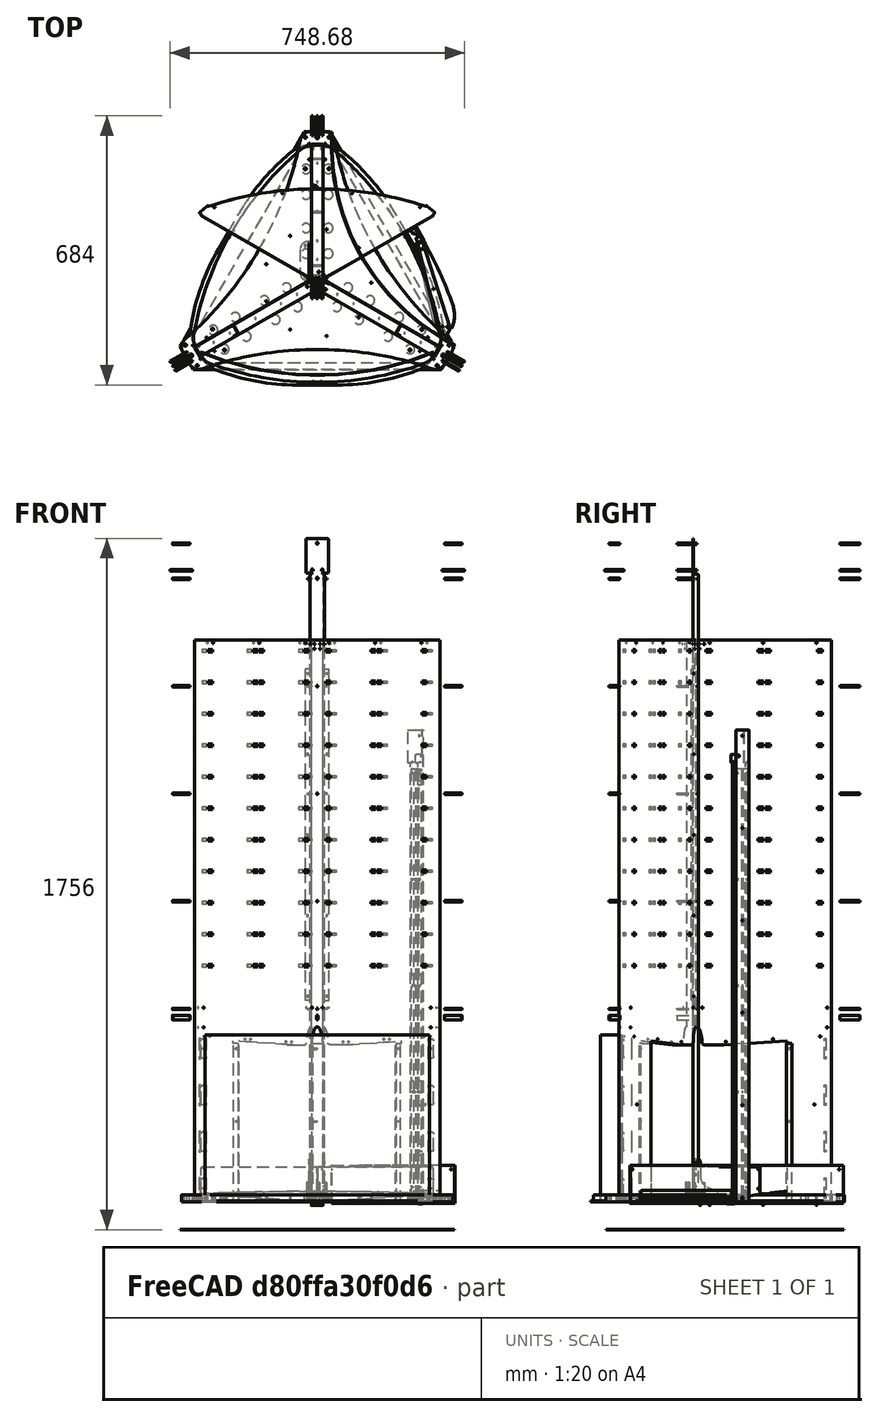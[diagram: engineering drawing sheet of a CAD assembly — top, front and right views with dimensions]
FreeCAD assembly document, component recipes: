
FREECAD ASSEMBLY — COMPONENT RECIPES ("composit_full_size3_door")

This assembly document has 79 components, labeled P0..P78 below (a component is one placed body or linked part). 75 of them carry a construction recipe — the FreeCAD feature program that regenerates the part from scratch, quoted from this document or its linked companion documents; the rest are supplied as boundary geometry only. No exploded tour is included for this assembly.
NOTE — document 2 of 3 of this assembly tour. The two overview renders and the header above are repeated from document 1; the component sections below continue where the previous document stopped.
COMPONENT P41 — recipe-attached ("top_bottom001", modeled in this document).
Construction recipe (the document's own serialized feature program — sketch geometry with constraints, then the solid features built on it; lengths are millimeters unless a unit is written):

FEATURE [PartDesign::SubShapeBinder] Binder007
  BindCopyOnChange = 0
  BindMode = 0
  ClaimChildren = true
  Fuse = false
  MakeFace = true
  OffsetFill = false
  OffsetIntersection = false
  OffsetJoinType = 0
  OffsetOpenResult = false
  PartialLoad = false
  Relative = false
  Support = -> [Compound011]
  _Version = 2
FEATURE [PartDesign::Pad] Pad005
  Direction = (0,0,1)
  Length = 3
  Length2 = 10
  Profile = -> Binder007
  Suppressed = false
  Type = 0
FEATURE [Sketcher::SketchObject] Sketch025
  AttachmentSupport = -> [XY_Plane007]
  FullyConstrained = true
  MapMode = 5
FEATURE [PartDesign::SubShapeBinder] Binder021
  BindCopyOnChange = 0
  BindMode = 0
  ClaimChildren = true
  Fuse = false
  MakeFace = true
  OffsetFill = false
  OffsetIntersection = false
  OffsetJoinType = 0
  OffsetOpenResult = false
  PartialLoad = false
  Relative = false
  Support = -> [Compound014]
  _Version = 2
FEATURE [PartDesign::Pocket] Pocket006
  BaseFeature = -> Pad005
  Direction = (0,0,-1)
  Length = 5
  Length2 = 5
  Midplane = true
  Profile = -> Binder021
  Suppressed = false
  Type = 1
FEATURE [Sketcher::SketchObject] Sketch027
  AttachmentSupport = -> [XY_Plane007]
  FullyConstrained = true
  MapMode = 5
  sketch-geometry (1):
    g0: Circle CenterX=0 CenterY=40 CenterZ=0 NormalX=0 NormalY=0 NormalZ=1 AngleXU=0 Radius=4
  constraints (3):
    c: PointOnObject(g0,g-2)
    c: Diameter(g0) = 8
    c: DistanceY(g0) = 40
FEATURE [PartDesign::SubShapeBinder] Binder023
  BindCopyOnChange = 0
  BindMode = 0
  ClaimChildren = true
  Context = -> Body004 [Binder023.]
  Fuse = false
  MakeFace = true
  OffsetFill = false
  OffsetIntersection = false
  OffsetJoinType = 0
  OffsetOpenResult = false
  PartialLoad = false
  Relative = true
  Support = -> [Clone005]
  _Version = 2
FEATURE [Sketcher::SketchObject] Sketch028
  AttachmentSupport = -> [XY_Plane007]
  ExternalGeometry = -> [Binder023]
  FullyConstrained = true
  MapMode = 5
  expr: Constraints[9] = <<Properties>>.rivet_d
  sketch-geometry (10):
    g0: Circle CenterX=0 CenterY=59 CenterZ=0 NormalX=0 NormalY=0 NormalZ=1 AngleXU=0 Radius=1.7
    g1: Circle CenterX=0 CenterY=106.372 CenterZ=0 NormalX=0 NormalY=0 NormalZ=1 AngleXU=0 Radius=1.7
    g2: Circle CenterX=0 CenterY=181.372 CenterZ=0 NormalX=0 NormalY=0 NormalZ=1 AngleXU=0 Radius=1.7
    g3: Circle CenterX=0 CenterY=256.372 CenterZ=0 NormalX=0 NormalY=0 NormalZ=1 AngleXU=0 Radius=1.7
    g4: Circle CenterX=0 CenterY=303.743 CenterZ=0 NormalX=0 NormalY=0 NormalZ=1 AngleXU=0 Radius=1.7
    g5: LineSegment StartX=28.3 StartY=73.8716 StartZ=0 EndX=28.3 EndY=106.372 EndZ=0
    g6: LineSegment StartX=28.3 StartY=106.372 StartZ=0 EndX=28.3 EndY=138.872 EndZ=0
    g7: LineSegment StartX=28.3 StartY=138.872 StartZ=0 EndX=28.3 EndY=181.372 EndZ=0
    g8: LineSegment StartX=28.3 StartY=181.372 StartZ=0 EndX=28.3 EndY=223.872 EndZ=0
    g9: LineSegment StartX=28.3 StartY=223.872 StartZ=0 EndX=28.3 EndY=256.372 EndZ=0
  constraints (24):
    c: PointOnObject(g0,g-2)
    c: PointOnObject(g1,g-2)
    c: PointOnObject(g2,g-2)
    c: PointOnObject(g3,g-2)
    c: DistanceY(g0) = 59
    c: Equal(g0, g1-g4) x4
    c: Diameter(g0) = 3.4
    c: Coincident(g5,g-3)
    c: Vertical(g5)
    c: Coincident(g5,g6)
    c: Coincident(g6,g-4)
    c: Coincident(g6,g7)
    c: Vertical(g7)
    c: Coincident(g7,g8)
    c: Coincident(g8,g-5)
    c: Coincident(g8,g9)
    c: Vertical(g9)
    c: Equal(g5,g6)
    c: Equal(g6,g9)
    c: Equal(g7,g8)
    c: Horizontal(g2,g7)
    c: Horizontal(g1,g5)
    c: Horizontal(g3,g9)
    c: Symmetric(g0,g4,g2)
FEATURE [PartDesign::Hole] Hole003
  BaseFeature = -> Pocket006
  CustomThreadClearance = 0
  Depth = 25
  DepthType = 0
  Diameter = 3.4
  DrillForDepth = false
  DrillPoint = 1
  DrillPointAngle = 118
  HoleCutCountersinkAngle = 90
  HoleCutCustomValues = false
  HoleCutDepth = 0
  HoleCutDiameter = 6.1
  HoleCutType = 0
  ModelThread = false
  Profile = -> Sketch028
  Reversed = true
  Suppressed = false
  Tapered = false
  TaperedAngle = 90
  ThreadClass = 0
  ThreadDepth = 25
  ThreadDepthType = 0
  ThreadDirection = 0
  ThreadFit = 0
  ThreadSize = 0
  ThreadType = 0
  Threaded = false
  UseCustomThreadClearance = false
  expr: Diameter = <<Properties>>.rivet_d
FEATURE [Part::Compound] Compound048  label="top_bottom_cut1"
  Links = -> [Extrude016,Extrude017]
FEATURE [Part::FeaturePython] Connect  label="top_bottom_cut1_refined"  # WARN: FeaturePython — macro-defined, semantics opaque (R4)
  Objects = -> [Compound048]
  Refine = true
  Tolerance = 0
FEATURE [PartDesign::Boolean] Boolean033
  BaseFeature = -> Hole003
  Group = -> [Compound081]
  Suppressed = false
  Type = 1
  UsePlacement = false
FEATURE [PartDesign::FeatureSubtractivePython] PDW_Common_Sub  # link proxy (typed FeaturePython)
  BaseFeature = -> Boolean033
  Body = Body004
  ClaimChildren = true
  EditPlacementAdjustments = false
  Enabled = 1
  LinkedObject = -> Connect
  MeshTolerance = 0.1
  PatternBaseOffset = 0
  PatternBaseScale = 1
  PatternBaseScaleXYZ = (1,1,1)
  PatternOffsetCut = false
  PatternOffsetIntersection = false
  PatternOffsetJoin = 0
  PatternOffsetMode = 0
  PatternOffsetSelfIntersection = false
  PatternOperation = 3
  PatternOperationDefault = Common
  PatternScaleCut = false
  PatternShapeOffset = 0
  PatternShapeScale = 1
  PatternShapeScaleXYZ = (1,1,1)
  PatternTool = -> Compound048
  PatternToolOffset = 0
  PatternToolScale = 1
  PatternToolScaleXYZ = (1,1,1)
  Refine = true
  RefineMesh = true
  ShapeManagement = 1
  ShowMeshProps = false
  ShowOffsetProps = false
  ShowScaleProps = false
  ShowWarnings = true
  Suppressed = false
  TipBase = -> Boolean033
  TipBaseOffset = 0
  TipBaseScale = 1
  TipBaseScaleXYZ = (1,1,1)
  TipOffsetCut = false
  TipOffsetIntersection = false
  TipOffsetJoin = 0
  TipOffsetMode = 0
  TipOffsetSelfIntersection = false
  TipOperation = 1
  TipOperationDefault = Common
  TipScaleCut = false
  TipShapeOffset = 0
  TipShapeScale = 1
  TipShapeScaleXYZ = (1,1,1)
  TipTool = -> Connect
  TipToolOffset = 0
  TipToolScale = 1
  TipToolScaleXYZ = (1,1,1)
  Type = Subtractive
  UsePatternBaseAddSubShape = false
  UsePatternToolAddSubShape = false
  UseTipBaseAddSubShape = true
  UseTipToolAddSubShape = true
  Version = 0.2023.08.13
FEATURE [PartDesign::CoordinateSystem] Local_CS029  label="dropper_fix_bottom_outer_LCS"
  AttacherType = Attacher::AttachEngine3D
  AttachmentSupport = -> [XY_Plane007]
  MapMode = 5
FEATURE [PartDesign::CoordinateSystem] Local_CS030  label="dropper_fix_bottom_inner_LCS"
  AttacherType = Attacher::AttachEngine3D
  AttachmentOffset = pos=(0,0,3) rot=(0,0,1;0rad)
  AttachmentSupport = -> [XY_Plane007]
  MapMode = 5
  Placement = pos=(0,0,3) rot=(0,0,1;0rad)
FEATURE [PartDesign::Body] Body004  label="dropper_fix_bottom"
  Group = -> [Binder007,Pad005,Sketch025,Binder021,Pocket006,Sketch027,Sketch028,Binder023,Hole003,Boolean033,PDW_Common_Sub,Compound048,Connect,Local_CS029,Local_CS030]
  Origin = -> Origin007
  Tip = -> PDW_Common_Sub
COMPONENT P42 — recipe-attached ("cap_outer_material_0.30ansi001", modeled in this document).
Construction recipe (the document's own serialized feature program — sketch geometry with constraints, then the solid features built on it; lengths are millimeters unless a unit is written):

FEATURE [PartDesign::SubShapeBinder] Binder012
  BindCopyOnChange = 0
  BindMode = 0
  ClaimChildren = true
  Fuse = false
  MakeFace = true
  OffsetFill = false
  OffsetIntersection = false
  OffsetJoinType = 0
  OffsetOpenResult = false
  PartialLoad = false
  Placement = pos=(0,0,40) rot=(0,0,1;0rad)
  Relative = false
  Support = -> [Compound012]
  _Version = 2
FEATURE [PartDesign::SubShapeBinder] Binder013
  BindCopyOnChange = 0
  BindMode = 0
  ClaimChildren = true
  Fuse = false
  MakeFace = true
  OffsetFill = false
  OffsetIntersection = false
  OffsetJoinType = 0
  OffsetOpenResult = false
  PartialLoad = false
  Placement = pos=(0,0,40) rot=(0,0,1;0rad)
  Relative = false
  Support = -> [Compound013]
  _Version = 2
FEATURE [PartDesign::FeaturePython] BaseBend007  # WARN: FeaturePython — macro-defined, semantics opaque (R4)
  BendSide = 1
  BendSketch = -> Binder012
  MidPlane = false
  Reverse = true
  Suppressed = false
  length = 100
  radius = 0.1
  thickness = 0.3
  expr: radius = composit_properties#<<Properties>>.bend_r
  expr: thickness = composit_properties#<<Properties>>.al_thickness
FEATURE [PartDesign::FeaturePython] Bend001  # WARN: FeaturePython — macro-defined, semantics opaque (R4)
  AutoMiter = false
  BaseFeature = -> BaseBend007
  BendType = 0
  LengthList = [47]
  LengthSpec = 1
  ReliefFactor = 0.7
  Suppressed = false
  UseReliefFactor = false
  angle = 90
  baseObject = -> BaseBend007 [Edge14,Edge30,Edge46,Edge62,Edge70,Edge86,Edge102,Edge116]
  bendAList = [90]
  extend1 = 0
  extend2 = 0
  gap1 = 0
  gap2 = 0
  invert = false
  kfactor = 0.5
  length = 47
  maxExtendDist = 5
  minGap = 0.1
  minReliefGap = 1
  miterangle1 = 0
  miterangle2 = 0
  offset = 0
  radius = 0.1
  reliefType = 0
  reliefd = 1
  reliefw = 0.8
  sketchflip = false
  sketchinvert = false
  unfold = false
  expr: radius = BaseBend007.radius
FEATURE [PartDesign::Pocket] Pocket002
  BaseFeature = -> Bend001
  Direction = (0,0,-1)
  Length = 5
  Length2 = 5
  Profile = -> Binder013 [Face1]
  Refine = true
  Reversed = true
  Suppressed = false
  Type = 1
FEATURE [PartDesign::SubShapeBinder] Binder014
  BindCopyOnChange = 0
  BindMode = 0
  ClaimChildren = true
  Context = -> Link012 [Binder014.]
  Fuse = false
  MakeFace = true
  OffsetFill = false
  OffsetIntersection = false
  OffsetJoinType = 0
  OffsetOpenResult = false
  PartialLoad = false
  Relative = true
  Support = -> [Sketch019]
  _Version = 2
FEATURE [Sketcher::SketchObject] Sketch020
  AttachmentSupport = -> [XY_Plane005]
  FullyConstrained = true
  MapMode = 5
  expr: Constraints[10] = composit_properties#<<Properties>>.bend_r + composit_properties#<<Properties>>.al_thickness
  sketch-geometry (5):
    g0: ArcOfCircle CenterX=0 CenterY=0.46188 CenterZ=0 NormalX=0 NormalY=0 NormalZ=1 AngleXU=0 Radius=5 StartAngle=0.523599 EndAngle=2.61799
    g1: LineSegment StartX=0 StartY=0 StartZ=0 EndX=4.53013 EndY=2.61547 EndZ=0
    g2: LineSegment StartX=4.53013 StartY=2.61547 StartZ=0 EndX=4.33013 EndY=2.96188 EndZ=0
    g3: LineSegment StartX=0 StartY=0 StartZ=0 EndX=-4.53013 EndY=2.61547 EndZ=0
    g4: LineSegment StartX=-4.53013 StartY=2.61547 StartZ=0 EndX=-4.33013 EndY=2.96188 EndZ=0
  constraints (13):
    c: PointOnObject(g0,g-2)
    c: Coincident(g1,g-1)
    c: Coincident(g2,g1)
    c: Coincident(g3,g1)
    c: Coincident(g4,g3)
    c: Perpendicular(g3,g4)
    c: Perpendicular(g1,g2)
    c: Tangent(g2,g0) = -1.5708
    c: Tangent(g4,g0) = 1.5708
    c: Equal(g4,g2)
    c: Distance(g2) = 0.4
    c: Diameter(g0) = 10
    c: Angle(g1,g3) = 2.0944
FEATURE [PartDesign::SubShapeBinder] Binder015
  BindCopyOnChange = 0
  BindMode = 0
  ClaimChildren = false
  Context = -> Link012 [Binder015.]
  Fuse = false
  MakeFace = true
  OffsetFill = false
  OffsetIntersection = false
  OffsetJoinType = 0
  OffsetOpenResult = false
  PartialLoad = false
  Relative = true
  Support = -> [Sketch002]
  _Version = 2
  expr: Support = <<dropper_fix_sketch>>._self
FEATURE [Sketcher::SketchObject] Sketch022  label="cap_outer_shape"
  AttachmentSupport = -> [YZ_Plane005]
  ExternalGeometry = -> [Binder012]
  FullyConstrained = true
  MapMode = 5
  Placement = pos=(0,0,0) rot=(0.57735,0.57735,0.57735;2.0944rad)
  expr: Constraints[11] = composit_properties#<<Properties>>.bend_r + composit_properties#<<Properties>>.al_thickness
  expr: Constraints[9] = composit_properties#<<Properties>>.bend_r + composit_properties#<<Properties>>.al_thickness + 0.01 mm
  sketch-geometry (5):
    g0: LineSegment StartX=351.882 StartY=40.41 StartZ=0 EndX=0 EndY=40.41 EndZ=0
    g1: LineSegment StartX=0 StartY=40.41 StartZ=0 EndX=0 EndY=0 EndZ=0
    g2: LineSegment StartX=0 StartY=0 StartZ=0 EndX=351.882 EndY=0 EndZ=0
    g3: LineSegment StartX=351.882 StartY=0 StartZ=0 EndX=351.882 EndY=40.41 EndZ=0
    g4: GeomPoint X=351.872 Y=40.4 Z=0
  constraints (14):
    c: Coincident(g0,g1)
    c: Coincident(g1,g2)
    c: Coincident(g2,g3)
    c: Coincident(g3,g0)
    c: Horizontal(g0)
    c: Horizontal(g2)
    c: Vertical(g1)
    c: Vertical(g3)
    c: Coincident(g1,g-1)
    c: DistanceY(g-3,g0) = 0.41
    c: DistanceX(g-3,g0) = 0.01
    c: DistanceY(g-3,g4) = 0.4
    c: Vertical(g-3,g4)
    c: DistanceY(g4) = 40.4  'height'
FEATURE [Part::FeaturePython] WireFilter002  # WARN: FeaturePython — macro-defined, semantics opaque (R4)
  AttacherType = Attacher::AttachEngine3D
  ClaimChildren = true
  ColorKeyCount = 8
  Colorize = true
  FaceMaker = 5
  FixNormal = false
  FollowSource = true
  InvertedFaceScale = 5
  MaxWires = 25
  Normal = (1,0,0)
  OffsetFill = false
  OffsetIntersection = false
  OffsetJoin = 0
  OffsetOpenResult = false
  Scale = (1,1,1)
  SelectEdges = false
  Source = -> Sketch022
  UniformScale = 1
  UseDefault = false
  UseSelected = true
  UseSelectedEdges = false
  Version = 0.2022.02.09
  WireOrder = [1]
FEATURE [PartDesign::SubShapeBinder] Binder132
  BindCopyOnChange = 0
  BindMode = 0
  ClaimChildren = true
  Fuse = false
  MakeFace = true
  OffsetFill = false
  OffsetIntersection = false
  OffsetJoinType = 0
  OffsetOpenResult = false
  PartialLoad = false
  Relative = false
  Support = -> [Sketch017]
  _Version = 2
FEATURE [PartDesign::Pocket] Pocket125
  BaseFeature = -> Pocket002
  Direction = (0,0,-1)
  Length = 5
  Length2 = 5
  Midplane = true
  Profile = -> Binder014
  Suppressed = false
  Type = 1
FEATURE [PartDesign::Pocket] Pocket003
  BaseFeature = -> Pocket125
  Direction = (0,0,-1)
  Length = 5
  Length2 = 5
  Midplane = true
  Profile = -> Sketch020
  ReferenceAxis = -> Sketch020 [N_Axis]
  Suppressed = false
  Type = 1
FEATURE [PartDesign::Mirrored] Mirrored
  BaseFeature = -> Pocket003
  MirrorPlane = -> YZ_Plane005
  Suppressed = false
FEATURE [PartDesign::Pocket] Pocket005
  BaseFeature = -> Mirrored
  Direction = (-1,0,0)
  Length = 5
  Length2 = 5
  Midplane = true
  Profile = -> WireFilter002
  Suppressed = false
  Type = 1
FEATURE [PartDesign::Boolean] Boolean032
  BaseFeature = -> Pocket005
  Group = -> [Compound080]
  Suppressed = false
  Type = 1
  UsePlacement = false
FEATURE [PartDesign::Body] Body002  label="cap_outer_material_0.30ansi"
  Group = -> [Binder012,Binder013,BaseBend007,Bend001,Pocket002,Binder014,Sketch020,Pocket125,Pocket003,Binder015,Mirrored,Sketch022,WireFilter002,Pocket005,Binder132,Boolean032]
  Origin = -> Origin005
  Tip = -> Boolean032
COMPONENT P43 — recipe-attached ("cap_inner2_material_0.30ansi001", modeled in this document).
Construction recipe (the document's own serialized feature program — sketch geometry with constraints, then the solid features built on it; lengths are millimeters unless a unit is written):

FEATURE [PartDesign::SubShapeBinder] Binder018
  BindCopyOnChange = 0
  BindMode = 0
  ClaimChildren = false
  Fuse = false
  MakeFace = true
  OffsetFill = false
  OffsetIntersection = false
  OffsetJoinType = 0
  OffsetOpenResult = false
  PartialLoad = false
  Relative = false
  Support = -> [Body002[BaseBend007.Binder012.Compound012.Part__Mirroring006.Sketch016.]]
  _Version = 2
FEATURE [PartDesign::SubShapeBinder] Binder019
  BindCopyOnChange = 0
  BindMode = 0
  ClaimChildren = false
  Fuse = false
  MakeFace = false
  OffsetFill = false
  OffsetIntersection = false
  OffsetJoinType = 0
  OffsetOpenResult = false
  PartialLoad = false
  Relative = false
  Support = -> [Sketch019]
  _Version = 2
FEATURE [Sketcher::SketchObject] Sketch024
  AttachmentSupport = -> [XY_Plane023]
  ExternalGeometry = -> [Binder019,Binder018]
  FullyConstrained = true
  MapMode = 5
  expr: Constraints[10] = composit_properties#<<Properties>>.thickness + composit_properties#<<Properties>>.al_thickness + composit_properties#<<Properties>>.bend_r
  sketch-geometry (5):
    g0: LineSegment StartX=-41.7 StartY=272.288 StartZ=0 EndX=-41.7 EndY=289.736 EndZ=0
    g1: LineSegment StartX=-41.7 StartY=289.736 StartZ=0 EndX=41.7 EndY=289.736 EndZ=0
    g2: LineSegment StartX=41.7 StartY=289.736 StartZ=0 EndX=41.7 EndY=272.288 EndZ=0
    g3: LineSegment StartX=41.7 StartY=272.288 StartZ=0 EndX=-41.7 EndY=272.288 EndZ=0
    g4: GeomPoint X=0 Y=281.012 Z=0
  constraints (13):
    c: Coincident(g0,g1)
    c: Coincident(g1,g2)
    c: Coincident(g2,g3)
    c: Coincident(g3,g0)
    c: Horizontal(g1)
    c: Horizontal(g3)
    c: Vertical(g0)
    c: Vertical(g2)
    c: Symmetric(g1,g0,g4)
    c: PointOnObject(g4,g-2)
    c: DistanceX(g1,g-4) = 3.4
    c: DistanceY(g2,g-3) = 5
    c: DistanceY(g1,g-4) = 3
FEATURE [PartDesign::FeaturePython] BaseBend008  # WARN: FeaturePython — macro-defined, semantics opaque (R4)
  BendSide = 0
  BendSketch = -> Sketch024
  MidPlane = false
  Reverse = false
  Suppressed = false
  length = 100
  radius = 0.1
  thickness = 0.3
  expr: radius = composit_properties#<<Properties>>.bend_r
  expr: thickness = composit_properties#<<Properties>>.al_thickness
FEATURE [Sketcher::SketchObject] Sketch217
  AttachmentSupport = -> [XY_Plane023]
  ExternalGeometry = -> [Sketch024,Binder018]
  FullyConstrained = true
  MapMode = 5
  sketch-geometry (6):
    g0: LineSegment StartX=41.7 StartY=289.736 StartZ=0 EndX=14.25 EndY=348.472 EndZ=0
    g1: LineSegment StartX=0 StartY=348.472 StartZ=0 EndX=14.25 EndY=348.472 EndZ=0
    g2: LineSegment StartX=14.25 StartY=351.872 StartZ=0 EndX=14.25 EndY=348.472 EndZ=0
    g3: LineSegment StartX=14.25 StartY=348.472 StartZ=0 EndX=17.3302 EndY=349.911 EndZ=0
    g4: LineSegment StartX=0 StartY=348.472 StartZ=0 EndX=0 EndY=289.736 EndZ=0
    g5: LineSegment StartX=0 StartY=289.736 StartZ=0 EndX=41.7 EndY=289.736 EndZ=0
  constraints (17):
    c: Coincident(g0,g-3)
    c: PointOnObject(g1,g-2)
    c: Coincident(g1,g0)
    c: Horizontal(g1)
    c: Coincident(g2,g0)
    c: Coincident(g2,g3)
    c: PointOnObject(g3,g-4)
    c: Perpendicular(g0,g3)
    c: Perpendicular(g1,g2)
    c: Equal(g3,g2)
    c: DistanceY(g2,g2) = 3.4
    c: Horizontal(g2,g-4)
    c: Coincident(g4,g1)
    c: PointOnObject(g4,g-3)
    c: Vertical(g4)
    c: Coincident(g5,g4)
    c: Coincident(g5,g0)
FEATURE [PartDesign::Pad] Pad033
  BaseFeature = -> BaseBend008
  Direction = (0,0,1)
  Length = 0.3
  Length2 = 10
  Profile = -> Sketch217
  ReferenceAxis = -> Sketch217 [N_Axis]
  Suppressed = false
  Type = 0
FEATURE [PartDesign::Mirrored] Mirrored016
  BaseFeature = -> Pad033
  MirrorPlane = -> Sketch217 [V_Axis]
  Originals = -> [Pad033]
  Suppressed = false
FEATURE [PartDesign::Hole] Hole002
  BaseFeature = -> Mirrored016
  CustomThreadClearance = 0
  Depth = 25
  DepthType = 0
  Diameter = 3.4
  DrillForDepth = false
  DrillPoint = 1
  DrillPointAngle = 118
  HoleCutCountersinkAngle = 90
  HoleCutCustomValues = false
  HoleCutDepth = 0
  HoleCutDiameter = 6.1
  HoleCutType = 0
  ModelThread = false
  Profile = -> Binder019
  Refine = true
  Reversed = true
  Suppressed = false
  Tapered = false
  TaperedAngle = 90
  ThreadClass = 0
  ThreadDepth = 25
  ThreadDepthType = 0
  ThreadDirection = 0
  ThreadFit = 0
  ThreadSize = 0
  ThreadType = 0
  Threaded = false
  UseCustomThreadClearance = false
  expr: Diameter = <<Properties>>.rivet_d
FEATURE [PartDesign::Body] Body016  label="cap_inner2_material_0.30ansi"
  Group = -> [Binder018,Binder019,Sketch024,BaseBend008,Sketch217,Pad033,Mirrored016,Hole002]
  Origin = -> Origin023
  Tip = -> Hole002
COMPONENT P44 — recipe-attached ("top_connector_material_0.30ansi001", modeled in this document).
Construction recipe (the document's own serialized feature program — sketch geometry with constraints, then the solid features built on it; lengths are millimeters unless a unit is written):

FEATURE [Sketcher::SketchObject] Sketch029  label="top_connector_base_sketch"
  AttachmentOffset = pos=(0,0,-35) rot=(0,0,1;0rad)
  AttachmentSupport = -> [XZ_Plane024]
  FullyConstrained = true
  MapMode = 5
  Placement = pos=(0,35,-7.8e-15) rot=(1,0,0;1.5708rad)
  expr: .Constraints.width = <<Properties>>.inner_width
  sketch-geometry (5):
    g0: LineSegment StartX=-11.5 StartY=-13 StartZ=0 EndX=-11.5 EndY=-1.95e-14 EndZ=0
    g1: LineSegment StartX=-11.5 StartY=-1.95e-14 StartZ=0 EndX=11.5 EndY=-1.95e-14 EndZ=0
    g2: LineSegment StartX=11.5 StartY=-1.95e-14 StartZ=0 EndX=11.5 EndY=-13 EndZ=0
    g3: LineSegment StartX=11.5 StartY=-13 StartZ=0 EndX=-11.5 EndY=-13 EndZ=0
    g4: GeomPoint X=-3.6e-15 Y=-6.5 Z=0
  constraints (13):
    c: Coincident(g0,g1)
    c: Coincident(g1,g2)
    c: Coincident(g2,g3)
    c: Coincident(g3,g0)
    c: Horizontal(g1)
    c: Horizontal(g3)
    c: Vertical(g0)
    c: Vertical(g2)
    c: Symmetric(g1,g0,g4)
    c: PointOnObject(g4,g-2)
    c: PointOnObject(g1,g-1)
    c: DistanceX(g1,g1) = 23  'width'
    c: DistanceY(g2,g2) = 13  'height'
FEATURE [PartDesign::FeaturePython] BaseBend009  # WARN: FeaturePython — macro-defined, semantics opaque (R4)
  BendSide = 0
  BendSketch = -> Sketch029
  MidPlane = false
  Reverse = true
  Suppressed = false
  length = 283.743
  radius = 0.1
  thickness = 0.3
  expr: radius = composit_properties#<<Properties>>.bend_r
  expr: thickness = composit_properties#<<Properties>>.al_thickness
FEATURE [PartDesign::SubShapeBinder] Binder029
  BindCopyOnChange = 0
  BindMode = 0
  ClaimChildren = false
  Context = -> Body017 [Binder029.]
  Fuse = false
  MakeFace = true
  OffsetFill = false
  OffsetIntersection = false
  OffsetJoinType = 0
  OffsetOpenResult = false
  PartialLoad = false
  Relative = true
  Support = -> [Sketch027]
  _Version = 2
  expr: Support = Sketch027._self
FEATURE [PartDesign::SubShapeBinder] Binder030
  BindCopyOnChange = 0
  BindMode = 0
  ClaimChildren = false
  Context = -> Body017 [Binder030.]
  Fuse = false
  MakeFace = true
  OffsetFill = false
  OffsetIntersection = false
  OffsetJoinType = 0
  OffsetOpenResult = false
  PartialLoad = false
  Relative = true
  Support = -> [Sketch028]
  _Version = 2
  expr: Support = Sketch028._self
FEATURE [PartDesign::Hole] Hole004
  BaseFeature = -> BaseBend009
  CustomThreadClearance = 0
  Depth = 25
  DepthType = 0
  Diameter = 3.4
  DrillForDepth = false
  DrillPoint = 1
  DrillPointAngle = 118
  HoleCutCountersinkAngle = 90
  HoleCutCustomValues = false
  HoleCutDepth = 0
  HoleCutDiameter = 6.1
  HoleCutType = 0
  ModelThread = false
  Profile = -> Binder030
  Suppressed = false
  Tapered = false
  TaperedAngle = 90
  ThreadClass = 0
  ThreadDepth = 25
  ThreadDepthType = 0
  ThreadDirection = 0
  ThreadFit = 0
  ThreadSize = 0
  ThreadType = 0
  Threaded = false
  UseCustomThreadClearance = false
  expr: Diameter = <<Properties>>.rivet_d
FEATURE [Sketcher::SketchObject] Sketch048
  AttachmentSupport = -> [YZ_Plane024]
  FullyConstrained = true
  MapMode = 5
  Placement = pos=(0,0,0) rot=(0.57735,0.57735,0.57735;2.0944rad)
  expr: Constraints[5] = -<<top_connector_base_sketch>>.Constraints.height
  expr: Constraints[7] = -<<top_connector_base_sketch>>.AttachmentOffset.Base.z
  sketch-geometry (3):
    g0: ArcOfCircle CenterX=42 CenterY=-6 CenterZ=0 NormalX=0 NormalY=0 NormalZ=1 AngleXU=0 Radius=7 StartAngle=3.14159 EndAngle=4.71239
    g1: LineSegment StartX=42 StartY=-13 StartZ=0 EndX=35 EndY=-13 EndZ=0
    g2: LineSegment StartX=35 StartY=-6 StartZ=0 EndX=35 EndY=-13 EndZ=0
  constraints (8):
    c: Horizontal(g1)
    c: Coincident(g2,g1)
    c: Vertical(g2)
    c: Tangent(g1,g0) = 1.5708
    c: Tangent(g2,g0) = -1.5708
    c: DistanceY(g1) = -13
    c: DistanceY(g0) = -6
    c: DistanceX(g1) = 35
FEATURE [PartDesign::Boolean] Boolean007
  BaseFeature = -> Hole004
  Group = -> [Compound078]
  Suppressed = false
  Type = 1
  UsePlacement = false
  expr: Group = <<top_connector_cut1>>._self
FEATURE [PartDesign::Pocket] Pocket027
  BaseFeature = -> Boolean007
  Direction = (-1,0,0)
  Length = 5
  Length2 = 5
  Midplane = true
  Profile = -> Sketch048
  ReferenceAxis = -> Sketch048 [N_Axis]
  Suppressed = false
  Type = 1
FEATURE [PartDesign::Body] Body017  label="top_connector_material_0.30ansi"
  Group = -> [Sketch029,BaseBend009,Binder029,Binder030,Hole004,Boolean007,Sketch048,Pocket027]
  Origin = -> Origin024
  Tip = -> Pocket027
COMPONENT P45 — recipe-attached ("cap_inner1_material_0.30ansi001", modeled in this document).
Construction recipe (the document's own serialized feature program — sketch geometry with constraints, then the solid features built on it; lengths are millimeters unless a unit is written):

FEATURE [PartDesign::SubShapeBinder] Binder016
  BindCopyOnChange = 0
  BindMode = 0
  ClaimChildren = true
  Fuse = false
  MakeFace = false
  OffsetFill = false
  OffsetIntersection = false
  OffsetJoinType = 0
  OffsetOpenResult = false
  PartialLoad = false
  Relative = false
  Support = -> [Sketch019]
  _Version = 2
FEATURE [PartDesign::SubShapeBinder] Binder020
  BindCopyOnChange = 0
  BindMode = 0
  ClaimChildren = false
  Context = -> Link015 [Binder020.]
  Fuse = false
  MakeFace = true
  OffsetFill = false
  OffsetIntersection = false
  OffsetJoinType = 0
  OffsetOpenResult = false
  PartialLoad = false
  Relative = true
  Support = -> [Body002[BaseBend007.Binder012.Compound012.Part__Mirroring006.Sketch016.]]
  _Version = 2
FEATURE [Sketcher::SketchObject] Sketch023
  AttachmentSupport = -> [XY_Plane006]
  ExternalGeometry = -> [Binder020]
  FullyConstrained = true
  MapMode = 5
  expr: Constraints[9] = composit_properties#<<Properties>>.thickness + composit_properties#<<Properties>>.bend_r + composit_properties#<<Properties>>.al_thickness
  sketch-geometry (5):
    g0: LineSegment StartX=41.7 StartY=29.0385 StartZ=0 EndX=-41.7 EndY=29.0385 EndZ=0
    g1: LineSegment StartX=-41.7 StartY=29.0385 StartZ=0 EndX=-41.7 EndY=58.0385 EndZ=0
    g2: LineSegment StartX=-41.7 StartY=58.0385 StartZ=0 EndX=41.7 EndY=58.0385 EndZ=0
    g3: LineSegment StartX=41.7 StartY=58.0385 StartZ=0 EndX=41.7 EndY=29.0385 EndZ=0
    g4: GeomPoint X=0 Y=43.5385 Z=0
  constraints (13):
    c: Coincident(g0,g1)
    c: Coincident(g1,g2)
    c: Coincident(g2,g3)
    c: Coincident(g3,g0)
    c: Horizontal(g0)
    c: Horizontal(g2)
    c: Vertical(g1)
    c: Vertical(g3)
    c: DistanceY(g-3,g0) = 3
    c: DistanceX(g0,g-3) = 3.4
    c: PointOnObject(g4,g-2)
    c: Symmetric(g2,g0,g4)
    c: DistanceY(g3,g3) = 29
FEATURE [PartDesign::Pad] Pad007
  Direction = (0,0,1)
  Length = 0.3
  Length2 = 10
  Profile = -> Sketch023
  ReferenceAxis = -> Sketch023 [N_Axis]
  Suppressed = false
  Type = 0
  expr: Length = composit_properties#<<Properties>>.al_thickness
FEATURE [PartDesign::FeaturePython] Bend002  label="cap_inner1_bend"  # WARN: FeaturePython — macro-defined, semantics opaque (R4)
  AutoMiter = true
  BaseFeature = -> Pad007
  BendType = 0
  LengthList = [31]
  LengthSpec = 0
  ReliefFactor = 0.7
  Suppressed = false
  UseReliefFactor = false
  angle = 90
  baseObject = -> Pad007 [Edge12,Edge7]
  bendAList = [90]
  extend1 = 0
  extend2 = 0
  gap1 = 0
  gap2 = 0
  invert = false
  kfactor = 0.5
  length = 31
  maxExtendDist = 5
  minGap = 0.1
  minReliefGap = 1
  miterangle1 = 0
  miterangle2 = 0
  offset = 0
  radius = 0.1
  reliefType = 0
  reliefd = 1
  reliefw = 0.8
  sketchflip = false
  sketchinvert = false
  unfold = false
  expr: length = <<cap_outer_shape>>.Constraints.height - composit_properties#<<Properties>>.thickness - composit_properties#<<Properties>>.al_thickness - composit_properties#<<Properties>>.bend_r - 6 mm
  expr: radius = BaseBend007.radius
FEATURE [PartDesign::Hole] Hole001
  BaseFeature = -> Bend002
  CustomThreadClearance = 0
  Depth = 25
  DepthType = 0
  Diameter = 3.4
  DrillForDepth = false
  DrillPoint = 1
  DrillPointAngle = 118
  HoleCutCountersinkAngle = 90
  HoleCutCustomValues = false
  HoleCutDepth = 0
  HoleCutDiameter = 6.1
  HoleCutType = 0
  ModelThread = false
  Profile = -> Binder016
  Reversed = true
  Suppressed = false
  Tapered = false
  TaperedAngle = 90
  ThreadClass = 0
  ThreadDepth = 25
  ThreadDepthType = 0
  ThreadDirection = 0
  ThreadFit = 0
  ThreadSize = 0
  ThreadType = 0
  Threaded = false
  UseCustomThreadClearance = false
  expr: Diameter = <<Properties>>.rivet_d
FEATURE [PartDesign::Body] Body003  label="cap_inner1_material_0.30ansi"
  Group = -> [Sketch023,Binder016,Binder020,Pad007,Bend002,Hole001]
  Origin = -> Origin006
  Tip = -> Hole001
COMPONENT P46 — same part as P37; its construction recipe is shown at P37.
COMPONENT P47 — recipe-attached ("part2_material_0.30ansi001", modeled in this document).
Construction recipe (the document's own serialized feature program — sketch geometry with constraints, then the solid features built on it; lengths are millimeters unless a unit is written):

FEATURE [PartDesign::SubShapeBinder] Binder001
  BindCopyOnChange = 0
  BindMode = 0
  ClaimChildren = true
  Context = -> Body001 [Binder001.]
  Fuse = false
  MakeFace = true
  OffsetFill = false
  OffsetIntersection = false
  OffsetJoinType = 0
  OffsetOpenResult = false
  PartialLoad = false
  Placement = pos=(0,0,0) rot=(0,0,1;4.18879rad)
  Relative = false
  Support = -> [Array001]
  _Version = 2
  expr: Support = <<2part_base>>._self
FEATURE [PartDesign::FeaturePython] BaseBend001  # WARN: FeaturePython — macro-defined, semantics opaque (R4)
  BendSide = 0
  BendSketch = -> Binder001
  MidPlane = false
  Reverse = false
  Suppressed = false
  length = 1428
  radius = 0.1
  thickness = 0.3
  expr: length = <<Properties>>.total_height
  expr: radius = composit_properties#<<Properties>>.bend_r
  expr: thickness = composit_properties#<<Properties>>.al_thickness
FEATURE [PartDesign::CoordinateSystem] Local_CS027  label="part2_bottom"
  AttacherType = Attacher::AttachEngine3D
  AttachmentOffset = pos=(0,0,0) rot=(0,0,1;2.0944rad)
  AttachmentSupport = -> [XY_Plane001]
  MapMode = 5
  Placement = pos=(0,0,0) rot=(0,0,1;2.0944rad)
FEATURE [PartDesign::CoordinateSystem] Local_CS028
  AttacherType = Attacher::AttachEngine3D
  AttachmentOffset = pos=(0,0,1428) rot=(0,0,1;0rad)
  AttachmentSupport = -> [Local_CS027]
  MapMode = 5
  Placement = pos=(0,0,1428) rot=(0,0,1;2.0944rad)
  expr: .AttachmentOffset.Base.z = <<Properties>>.total_height
FEATURE [PartDesign::Boolean] Boolean
  BaseFeature = -> BaseBend001
  Group = -> [Compound021]
  Refine = true
  Suppressed = false
  Type = 1
  UsePlacement = false
  expr: Group = <<part2_cut1>>._self
FEATURE [PartDesign::Boolean] Boolean003
  BaseFeature = -> Boolean
  Group = -> [Compound007]
  Refine = true
  Suppressed = false
  Type = 0
  UsePlacement = false
  expr: Group = <<part2_fuse1>>._self
FEATURE [PartDesign::Boolean] Boolean006
  BaseFeature = -> Boolean003
  Group = -> [Compound025]
  Suppressed = false
  Type = 1
  UsePlacement = false
  expr: Group = <<part2_cut2>>._self
FEATURE [PartDesign::Body] Body001  label="part2_material_0.30ansi"
  Group = -> [Binder001,BaseBend001,Boolean,Boolean003,Boolean006,Local_CS027,Local_CS028]
  Origin = -> Origin001
  Tip = -> Boolean006
COMPONENT P48 — recipe-attached ("bot_hor_amplifier_material_0.30ansi001", modeled in this document).
Construction recipe (the document's own serialized feature program — sketch geometry with constraints, then the solid features built on it; lengths are millimeters unless a unit is written):

FEATURE [Sketcher::SketchObject] Sketch049
  AttachmentSupport = -> [YZ_Plane030]
  FullyConstrained = true
  MapMode = 5
  Placement = pos=(0,0,0) rot=(0.57735,0.57735,0.57735;2.0944rad)
  expr: Constraints[11] = <<Properties>>.inner_width
  sketch-geometry (5):
    g0: LineSegment StartX=-11.5 StartY=-14 StartZ=0 EndX=-11.5 EndY=0 EndZ=0
    g1: LineSegment StartX=-11.5 StartY=0 StartZ=0 EndX=11.5 EndY=0 EndZ=0
    g2: LineSegment StartX=11.5 StartY=0 StartZ=0 EndX=11.5 EndY=-14 EndZ=0
    g3: LineSegment StartX=11.5 StartY=-14 StartZ=0 EndX=-11.5 EndY=-14 EndZ=0
    g4: GeomPoint X=0 Y=-7 Z=0
  constraints (13):
    c: Coincident(g0,g1)
    c: Coincident(g1,g2)
    c: Coincident(g2,g3)
    c: Coincident(g3,g0)
    c: Horizontal(g1)
    c: Horizontal(g3)
    c: Vertical(g0)
    c: Vertical(g2)
    c: Symmetric(g1,g0,g4)
    c: PointOnObject(g4,g-2)
    c: PointOnObject(g1,g-1)
    c: DistanceX(g1,g1) = 23
    c: DistanceY(g2) = -14
FEATURE [PartDesign::FeaturePython] BaseBend019  # WARN: FeaturePython — macro-defined, semantics opaque (R4)
  BendSide = 0
  BendSketch = -> Sketch049
  MidPlane = true
  Reverse = false
  Suppressed = false
  length = 250
  radius = 0.1
  thickness = 0.3
FEATURE [PartDesign::Boolean] Boolean009
  BaseFeature = -> BaseBend019
  Group = -> [Extrude008]
  Suppressed = false
  Type = 1
  UsePlacement = false
  expr: Group = <<bot_hor_amplifier_extrude>>._self
FEATURE [PartDesign::Body] Body068  label="bot_hor_amplifier_material_0.30ansi"
  Group = -> [BaseBend019,Sketch049,Boolean009]
  Origin = -> Origin030
  Tip = -> Boolean009
COMPONENT P49 — recipe-attached ("star_material_0.30ansi001", modeled in this document).
Construction recipe (the document's own serialized feature program — sketch geometry with constraints, then the solid features built on it; lengths are millimeters unless a unit is written):

FEATURE [Sketcher::SketchObject] Sketch032
  AttachmentSupport = -> [XZ_Plane025]
  FullyConstrained = true
  MapMode = 5
  Placement = pos=(0,0,0) rot=(1,0,0;1.5708rad)
  expr: Constraints[11] = <<Properties>>.inner_width
  sketch-geometry (5):
    g0: LineSegment StartX=-11.5 StartY=-12 StartZ=0 EndX=-11.5 EndY=-2.84e-14 EndZ=0
    g1: LineSegment StartX=-11.5 StartY=-2.84e-14 StartZ=0 EndX=11.5 EndY=-2.84e-14 EndZ=0
    g2: LineSegment StartX=11.5 StartY=-2.84e-14 StartZ=0 EndX=11.5 EndY=-12 EndZ=0
    g3: LineSegment StartX=11.5 StartY=-12 StartZ=0 EndX=-11.5 EndY=-12 EndZ=0
    g4: GeomPoint X=-5.1e-15 Y=-6 Z=0
  constraints (13):
    c: Coincident(g0,g1)
    c: Coincident(g1,g2)
    c: Coincident(g2,g3)
    c: Coincident(g3,g0)
    c: Horizontal(g1)
    c: Horizontal(g3)
    c: Vertical(g0)
    c: Vertical(g2)
    c: Symmetric(g1,g0,g4)
    c: PointOnObject(g4,g-2)
    c: PointOnObject(g1,g-1)
    c: DistanceX(g1,g1) = 23
    c: DistanceY(g2,g2) = 12
FEATURE [PartDesign::FeaturePython] BaseBend010  # WARN: FeaturePython — macro-defined, semantics opaque (R4)
  BendSide = 0
  BendSketch = -> Sketch032
  MidPlane = false
  Reverse = true
  Suppressed = false
  length = 35
  radius = 0.1
  thickness = 0.3
  expr: radius = composit_properties#<<Properties>>.bend_r
  expr: thickness = composit_properties#<<Properties>>.al_thickness
FEATURE [Sketcher::SketchObject] Sketch033
  AttachmentSupport = -> [XY_Plane025]
  FullyConstrained = true
  MapMode = 5
  expr: Constraints[6] = composit_properties#<<Properties>>.bend_r + composit_properties#<<Properties>>.al_thickness
  expr: Constraints[7] = <<Properties>>.inner_width / 2
  sketch-geometry (7):
    g0: LineSegment StartX=0 StartY=-1.289e-13 StartZ=0 EndX=11.1 EndY=6.40859 EndZ=0
    g1: LineSegment StartX=11.5 StartY=0 StartZ=0 EndX=0 EndY=-1.289e-13 EndZ=0
    g2: LineSegment StartX=11.1 StartY=6.40859 StartZ=0 EndX=11.1 EndY=8.33953 EndZ=0
    g3: LineSegment StartX=11.1 StartY=8.33953 StartZ=0 EndX=11.5 EndY=8.33953 EndZ=0
    g4: GeomPoint X=11.5 Y=6.63953 Z=0
    g5: LineSegment StartX=11.5 StartY=8.33953 StartZ=0 EndX=11.5 EndY=6.63953 EndZ=0
    g6: LineSegment StartX=11.5 StartY=6.63953 StartZ=0 EndX=11.5 EndY=0 EndZ=0
  constraints (18):
    c: Coincident(g-1,g0)
    c: Coincident(g0,g2)
    c: Coincident(g3,g5)
    c: PointOnObject(g6,g-1)
    c: Coincident(g6,g1)
    c: Coincident(g1,g0)
    c: DistanceX(g2,g3) = 0.4
    c: DistanceX(g1,g1) = 11.5
    c: Coincident(g2,g3)
    c: Horizontal(g3)
    c: Vertical(g2)
    c: PointOnObject(g4,g0)
    c: DistanceY(g4,g5) = 1.7
    c: Angle(g0) = 0.523599
    c: Coincident(g5,g6)
    c: Vertical(g5)
    c: Vertical(g6)
    c: Coincident(g5,g4)
FEATURE [PartDesign::Pocket] Pocket018
  BaseFeature = -> BaseBend010
  Direction = (0,0,-1)
  Length = 5
  Length2 = 5
  Profile = -> Sketch033
  ReferenceAxis = -> Sketch033 [N_Axis]
  Suppressed = false
  Type = 1
FEATURE [PartDesign::Mirrored] Mirrored001
  BaseFeature = -> Pocket018
  MirrorPlane = -> Sketch033 [V_Axis]
  Originals = -> [Pocket018]
  Suppressed = false
FEATURE [Sketcher::SketchObject] Sketch034
  AttachmentSupport = -> [YZ_Plane025]
  ExternalGeometry = -> [Sketch033]
  FullyConstrained = false
  MapMode = 5
  Placement = pos=(0,0,0) rot=(0.57735,0.57735,0.57735;2.0944rad)
  sketch-geometry (4):
    g0: LineSegment StartX=6.63953 StartY=-25.0734 StartZ=0 EndX=22.8156 EndY=-25.0734 EndZ=0
    g1: LineSegment StartX=22.8156 StartY=-25.0734 StartZ=0 EndX=8.57047 EndY=-0.4 EndZ=0
    g2: LineSegment StartX=6.63953 StartY=-0.4 StartZ=0 EndX=6.63953 EndY=-25.0734 EndZ=0
    g3: LineSegment StartX=6.63953 StartY=-0.4 StartZ=0 EndX=8.57047 EndY=-0.4 EndZ=0
  constraints (11):
    c: Coincident(g2,g0)
    c: Horizontal(g0)
    c: Coincident(g0,g1)
    c: Vertical(g2)
    c: Coincident(g3,g2)
    c: Coincident(g3,g1)
    c: Horizontal(g3)
    c: Angle(g1) = 2.0944
    c: DistanceY(g2) = -0.4
    c: PointOnObject(g-3,g2)
    c: PointOnObject(g-3,g1)
FEATURE [PartDesign::Pocket] Pocket019
  BaseFeature = -> Mirrored001
  Direction = (-1,0,0)
  Length = 5
  Length2 = 5
  Midplane = true
  Profile = -> Sketch034
  ReferenceAxis = -> Sketch034 [N_Axis]
  Suppressed = false
  Type = 1
FEATURE [Sketcher::SketchObject] Sketch036
  AttachmentSupport = -> [XY_Plane025]
  FullyConstrained = true
  MapMode = 5
  sketch-geometry (1):
    g0: Circle CenterX=0 CenterY=25 CenterZ=0 NormalX=0 NormalY=0 NormalZ=1 AngleXU=0 Radius=3
  constraints (3):
    c: PointOnObject(g0,g-2)
    c: DistanceY(g0) = 25
    c: Diameter(g0) = 6
FEATURE [PartDesign::Pocket] Pocket021
  BaseFeature = -> Pocket019
  Direction = (0,0,-1)
  Length = 5
  Length2 = 5
  Profile = -> Sketch036
  ReferenceAxis = -> Sketch036 [N_Axis]
  Suppressed = false
  Type = 0
FEATURE [Sketcher::SketchObject] Sketch045
  AttachmentSupport = -> [YZ_Plane025]
  FullyConstrained = true
  MapMode = 5
  Placement = pos=(0,0,0) rot=(0.57735,0.57735,0.57735;2.0944rad)
  expr: Constraints[0] = <<BaseBend010>>.length
  sketch-geometry (5):
    g0: ArcOfCircle CenterX=30 CenterY=-7 CenterZ=0 NormalX=0 NormalY=0 NormalZ=1 AngleXU=0 Radius=5 StartAngle=4.71239 EndAngle=6.28319
    g1: LineSegment StartX=35 StartY=-7 StartZ=0 EndX=35 EndY=-25 EndZ=0
    g2: LineSegment StartX=30 StartY=-12 StartZ=0 EndX=0 EndY=-12 EndZ=0
    g3: LineSegment StartX=35 StartY=-25 StartZ=0 EndX=0 EndY=-25 EndZ=0
    g4: LineSegment StartX=0 StartY=-25 StartZ=0 EndX=0 EndY=-12 EndZ=0
  constraints (14):
    c: DistanceX(g0) = 35
    c: Vertical(g1)
    c: Tangent(g1,g0) = 1.5708
    c: PointOnObject(g2,g-2)
    c: Horizontal(g2)
    c: Coincident(g3,g1)
    c: PointOnObject(g3,g-2)
    c: Horizontal(g3)
    c: Coincident(g4,g3)
    c: Coincident(g4,g2)
    c: Tangent(g2,g0) = 1.5708
    c: DistanceY(g0) = -7
    c: DistanceY(g3) = -25
    c: Radius(g0) = 5
FEATURE [PartDesign::Pocket] Pocket026
  BaseFeature = -> Pocket021
  Direction = (-1,0,0)
  Length = 5
  Length2 = 5
  Midplane = true
  Profile = -> Sketch045
  ReferenceAxis = -> Sketch045 [N_Axis]
  Suppressed = false
  Type = 1
FEATURE [PartDesign::Boolean] Boolean004
  BaseFeature = -> Pocket026
  Group = -> [Compound077]
  Suppressed = false
  Type = 1
  UsePlacement = false
  expr: Group = <<star_amplifier_cut1>>._self
FEATURE [PartDesign::FeatureAdditivePython] PDW_Common_Add002  # link proxy (typed FeaturePython)
  BaseFeature = -> Boolean004
  Body = Body018
  ClaimChildren = false
  EditPlacementAdjustments = false
  Enabled = 1
  LinkedObject = -> Boolean004
  MeshTolerance = 0.1
  PatternBase = -> Pocket026
  PatternBaseOffset = 0
  PatternBaseScale = 1
  PatternBaseScaleXYZ = (1,1,1)
  PatternOffsetCut = false
  PatternOffsetIntersection = false
  PatternOffsetJoin = 0
  PatternOffsetMode = 0
  PatternOffsetSelfIntersection = false
  PatternOperation = 3
  PatternOperationDefault = Common
  PatternScaleCut = false
  PatternShapeOffset = 0
  PatternShapeScale = 1
  PatternShapeScaleXYZ = (1,1,1)
  PatternTool = -> Boolean004
  PatternToolOffset = 0
  PatternToolScale = 1
  PatternToolScaleXYZ = (1,1,1)
  RefineMesh = true
  ShapeManagement = 0
  ShowMeshProps = false
  ShowOffsetProps = false
  ShowScaleProps = false
  ShowWarnings = true
  Suppressed = false
  TipBase = -> Pocket026
  TipBaseOffset = 0
  TipBaseScale = 1
  TipBaseScaleXYZ = (1,1,1)
  TipOffsetCut = false
  TipOffsetIntersection = false
  TipOffsetJoin = 0
  TipOffsetMode = 0
  TipOffsetSelfIntersection = false
  TipOperation = 2
  TipOperationDefault = Common
  TipScaleCut = false
  TipShapeOffset = 0
  TipShapeScale = 1
  TipShapeScaleXYZ = (1,1,1)
  TipTool = -> Boolean004
  TipToolOffset = 0
  TipToolScale = 1
  TipToolScaleXYZ = (1,1,1)
  Type = Additive
  UsePatternBaseAddSubShape = false
  UsePatternToolAddSubShape = true
  UseTipBaseAddSubShape = false
  UseTipToolAddSubShape = true
  Version = 0.2023.08.13
FEATURE [PartDesign::PolarPattern] PolarPattern008
  Angle = 360
  Axis = -> Z_Axis025
  BaseFeature = -> PDW_Common_Add002
  Mode = 0
  Occurrences = 3
  Offset = 120
  Originals = -> [PDW_Common_Add002]
  Refine = true
  Suppressed = false
FEATURE [PartDesign::Body] Body018  label="star_material_0.30ansi"
  Group = -> [Sketch032,BaseBend010,Sketch033,Pocket018,Mirrored001,Sketch034,Pocket019,Sketch036,Pocket021,Sketch045,Pocket026,Boolean004,PDW_Common_Add002,PolarPattern008]
  Origin = -> Origin025
  Placement = pos=(0,0,1428) rot=(0,0,1;0rad)
  Tip = -> PolarPattern008
  expr: .Placement.Base.z = <<Properties>>.total_height
COMPONENT P50 — recipe-attached ("plexiglass_outer_material_0.30ansi001", modeled in this document).
Construction recipe (the document's own serialized feature program — sketch geometry with constraints, then the solid features built on it; lengths are millimeters unless a unit is written):

FEATURE [PartDesign::SubShapeBinder] Binder037
  BindCopyOnChange = 0
  BindMode = 0
  ClaimChildren = true
  Context = -> Body072 [Binder037.]
  Fuse = false
  MakeFace = true
  OffsetFill = false
  OffsetIntersection = false
  OffsetJoinType = 0
  OffsetOpenResult = false
  PartialLoad = false
  Relative = false
  Support = -> [Compound036]
  _Version = 2
FEATURE [PartDesign::FeaturePython] BaseBend018  # WARN: FeaturePython — macro-defined, semantics opaque (R4)
  BendSide = 1
  BendSketch = -> Binder037
  MidPlane = false
  Placement = pos=(0,0,1596) rot=(0,0,1;0rad)
  Reverse = true
  Suppressed = false
  length = 1203
  radius = 1
  thickness = 1.5
FEATURE [PartDesign::FeaturePython] Extend  # WARN: FeaturePython — macro-defined, semantics opaque (R4)
  BaseFeature = -> BaseBend018
  Offset = 0.02
  Refine = true
  Suppressed = false
  UseSubtraction = false
  baseObject = -> BaseBend018 [Face32]
  gap1 = 0
  gap2 = 0
  length = 0
FEATURE [PartDesign::Boolean] Boolean013
  BaseFeature = -> Extend
  Group = -> [Populate018]
  Suppressed = false
  Type = 1
  UsePlacement = false
FEATURE [PartDesign::Body] Body072  label="plexiglass_outer_material_0.30ansi"
  Group = -> [Binder037,BaseBend018,Extend,Boolean013]
  Origin = -> Origin035
  Tip = -> Extend
COMPONENT P51 — recipe-attached ("pillar_bottom_material_0.30ansi001", modeled in this document).
Construction recipe (the document's own serialized feature program — sketch geometry with constraints, then the solid features built on it; lengths are millimeters unless a unit is written):

FEATURE [Sketcher::SketchObject] Sketch010  label="pillar_bottom_BaseSketch"
  AttachmentSupport = -> [YZ_Plane015]
  FullyConstrained = true
  MapMode = 5
  Placement = pos=(0,0,0) rot=(0.57735,0.57735,0.57735;2.0944rad)
  sketch-geometry (2):
    g0: LineSegment StartX=-25 StartY=0 StartZ=0 EndX=0 EndY=0 EndZ=0
    g1: LineSegment StartX=0 StartY=0 StartZ=0 EndX=0 EndY=110 EndZ=0
  constraints (6):
    c: PointOnObject(g0,g-1)
    c: Coincident(g0,g-1)
    c: Coincident(g0,g1)
    c: PointOnObject(g1,g-2)
    c: DistanceX(g0,g0) = 25  'leg_length'
    c: DistanceY(g1) = 110  'height'
FEATURE [PartDesign::FeaturePython] BaseBend005  label="pillar_bottom_BaseBend"  # WARN: FeaturePython — macro-defined, semantics opaque (R4)
  BendSide = 0
  BendSketch = -> Sketch010
  MidPlane = true
  Reverse = true
  Suppressed = false
  length = 101
  radius = 2
  thickness = 2
FEATURE [Sketcher::SketchObject] Sketch011  label="pillar_bottom_cut_vert"
  AttachmentSupport = -> [XZ_Plane015]
  FullyConstrained = true
  MapMode = 5
  Placement = pos=(0,0,0) rot=(1,0,0;1.5708rad)
  expr: Constraints[15] = <<pillar_bottom_BaseBend>>.length
  expr: Constraints[16] = <<pillar_bottom_BaseBend>>.radius + <<pillar_bottom_BaseBend>>.thickness
  expr: Constraints[27] = <<pillar_base_sketch>>.Constraints.length - 4 mm
  sketch-geometry (15):
    g0: LineSegment StartX=-50.5 StartY=0 StartZ=0 EndX=-50.5 EndY=75 EndZ=0
    g1: LineSegment StartX=-45.5 StartY=80 StartZ=0 EndX=-40.5 EndY=80 EndZ=0
    g2: LineSegment StartX=50.5 StartY=4 StartZ=0 EndX=50.5 EndY=0 EndZ=0
    g3: LineSegment StartX=50.5 StartY=0 StartZ=0 EndX=-50.5 EndY=0 EndZ=0
    g4: ArcOfCircle CenterX=-45.5 CenterY=75 CenterZ=0 NormalX=0 NormalY=0 NormalZ=1 AngleXU=0 Radius=5 StartAngle=1.5708 EndAngle=3.14159
    g5: GeomPoint X=-50.5 Y=80 Z=0
    g6: ArcOfCircle CenterX=-40.5 CenterY=75 CenterZ=0 NormalX=0 NormalY=0 NormalZ=1 AngleXU=0 Radius=5 StartAngle=0 EndAngle=1.5708
    g7: GeomPoint X=-35.5 Y=80 Z=0
    g8: ArcOfCircle CenterX=45.5 CenterY=4 CenterZ=0 NormalX=0 NormalY=0 NormalZ=1 AngleXU=0 Radius=5 StartAngle=0 EndAngle=1.13485
    g9: GeomPoint X=50.5 Y=7.18672 Z=0
    g10: LineSegment StartX=-35.5 StartY=75 StartZ=0 EndX=-35.5 EndY=64.709 EndZ=0
    g11: LineSegment StartX=-19.6724 StartY=39.8753 StartZ=0 EndX=47.6113 EndY=8.53236 EndZ=0
    g12: ArcOfCircle CenterX=-8.10401 CenterY=64.709 CenterZ=0 NormalX=0 NormalY=0 NormalZ=1 AngleXU=0 Radius=27.396 StartAngle=3.14159 EndAngle=4.27645
    g13: GeomPoint X=-19.6724 Y=39.8753 Z=0
    g14: GeomPoint X=-13.5 Y=37 Z=0
  constraints (34):
    c: PointOnObject(g0,g-1)
    c: Vertical(g0)
    c: Horizontal(g1)
    c: Vertical(g2)
    c: Coincident(g2,g3)
    c: Coincident(g3,g0)
    c: PointOnObject(g5,g0)
    c: PointOnObject(g5,g1)
    c: Tangent(g0,g4) = 1.5708
    c: Tangent(g1,g4) = 1.5708
    c: PointOnObject(g7,g1)
    c: Tangent(g1,g6) = 1.5708
    c: PointOnObject(g9,g2)
    c: Tangent(g2,g8) = 1.5708
    c: Symmetric(g0,g2,g-2)
    c: DistanceX(g3,g3) = 101
    c: DistanceY(g2) = 4
    c: DistanceY(g5) = 80  'height'
    c: Radius(g4) = 5
    c: Radius(g8) = 5
    c: Equal(g4,g6)
    c: PointOnObject(g7,g10)
    c: PointOnObject(g9,g11)
    c: Vertical(g10)
    c: Tangent(g10,g6) = 1.5708
    c: Tangent(g12,g10) = -1.5708
    c: Tangent(g12,g11) = -1.5708
    c: DistanceX(g5,g7) = 15
    c: Tangent(g11,g8) = 1.5708
    c: Coincident(g11,g13)
    c: PointOnObject(g14,g11)
    c: DistanceY(g14) = 37
    c: DistanceX(g0,g14) = 37
    c: DistanceX(g11) = -19.6724
FEATURE [Sketcher::SketchObject] Sketch012
  AttachmentSupport = -> [XY_Plane015]
  FullyConstrained = true
  MapMode = 5
  expr: Constraints[18] = <<pillar_bottom_BaseSketch>>.Constraints.leg_length
  expr: Constraints[20] = <<pillar_bottom_BaseBend>>.radius + <<pillar_bottom_BaseBend>>.thickness
  expr: Constraints[9] = <<pillar_bottom_BaseBend>>.length
  sketch-geometry (9):
    g0: LineSegment StartX=-50.5 StartY=-4 StartZ=0 EndX=-50.5 EndY=0 EndZ=0
    g1: LineSegment StartX=-50.5 StartY=0 StartZ=0 EndX=50.5 EndY=0 EndZ=0
    g2: LineSegment StartX=50.5 StartY=0 StartZ=0 EndX=50.5 EndY=-4 EndZ=0
    g3: LineSegment StartX=29.5 StartY=-25 StartZ=0 EndX=-29.5 EndY=-25 EndZ=0
    g4: GeomPoint X=0 Y=-12.5 Z=0
    g5: ArcOfCircle CenterX=29.5 CenterY=-4 CenterZ=0 NormalX=0 NormalY=0 NormalZ=1 AngleXU=0 Radius=21 StartAngle=4.71239 EndAngle=6.28319
    g6: GeomPoint X=50.5 Y=-25 Z=0
    g7: ArcOfCircle CenterX=-29.5 CenterY=-4 CenterZ=0 NormalX=0 NormalY=0 NormalZ=1 AngleXU=0 Radius=21 StartAngle=3.14159 EndAngle=4.71239
    g8: GeomPoint X=-50.5 Y=-25 Z=0
  constraints (21):
    c: Coincident(g0,g1)
    c: Coincident(g1,g2)
    c: Horizontal(g1)
    c: Horizontal(g3)
    c: Vertical(g0)
    c: Vertical(g2)
    c: Symmetric(g1,g8,g4)
    c: PointOnObject(g4,g-2)
    c: PointOnObject(g1,g-1)
    c: DistanceX(g1,g1) = 101
    c: PointOnObject(g6,g2)
    c: PointOnObject(g6,g3)
    c: Tangent(g2,g5) = 1.5708
    c: Tangent(g3,g5) = 1.5708
    c: PointOnObject(g8,g0)
    c: PointOnObject(g8,g3)
    c: Tangent(g0,g7) = 1.5708
    c: Tangent(g3,g7) = 1.5708
    c: DistanceY(g6,g-1) = 25
    c: Equal(g7,g5)
    c: DistanceY(g2,g-1) = 4
FEATURE [Part::FeaturePython] WireFilter  # WARN: FeaturePython — macro-defined, semantics opaque (R4)
  AttacherType = Attacher::AttachEngine3D
  ClaimChildren = true
  ColorKeyCount = 8
  Colorize = true
  FaceMaker = 5
  FixNormal = false
  FollowSource = true
  InvertedFaceScale = 20
  MaxWires = 25
  Normal = (0,1,-2e-16)
  OffsetFill = false
  OffsetIntersection = false
  OffsetJoin = 0
  OffsetOpenResult = false
  Scale = (1,1,1)
  SelectEdges = false
  Source = -> Sketch011
  UniformScale = 1
  UseDefault = false
  UseSelected = true
  UseSelectedEdges = false
  Version = 0.2022.02.09
  WireOrder = [1]
FEATURE [Part::FeaturePython] WireFilter001  # WARN: FeaturePython — macro-defined, semantics opaque (R4)
  AttacherType = Attacher::AttachEngine3D
  ClaimChildren = true
  ColorKeyCount = 8
  Colorize = true
  FaceMaker = 5
  FixNormal = false
  FollowSource = true
  InvertedFaceScale = 5
  MaxWires = 25
  Normal = (0,0,1)
  OffsetFill = false
  OffsetIntersection = false
  OffsetJoin = 0
  OffsetOpenResult = false
  Scale = (1,1,1)
  SelectEdges = false
  Source = -> Sketch012
  UniformScale = 1
  UseDefault = false
  UseSelected = true
  UseSelectedEdges = false
  Version = 0.2022.02.09
  WireOrder = [1]
FEATURE [PartDesign::Pocket] Pocket
  BaseFeature = -> BaseBend005
  Direction = (0,-1,2e-16)
  Length = 5
  Length2 = 5
  Profile = -> WireFilter
  Suppressed = false
  Type = 1
FEATURE [PartDesign::Pocket] Pocket001
  BaseFeature = -> Pocket
  Direction = (0,0,-1)
  Length = 5
  Length2 = 5
  Profile = -> WireFilter001
  Reversed = true
  Suppressed = false
  Type = 1
FEATURE [Sketcher::SketchObject] Sketch070
  AttachmentSupport = -> [XY_Plane015]
  FullyConstrained = true
  MapMode = 5
  sketch-geometry (2):
    g0: Circle CenterX=-40 CenterY=-12 CenterZ=0 NormalX=0 NormalY=0 NormalZ=1 AngleXU=0 Radius=2.75
    g1: Circle CenterX=40 CenterY=-12 CenterZ=0 NormalX=0 NormalY=0 NormalZ=1 AngleXU=0 Radius=2.75
  constraints (5):
    c: Equal(g1,g0)
    c: Diameter(g1) = 5.5
    c: Symmetric(g0,g1,g-2)
    c: DistanceX(g0,g1) = 80
    c: DistanceY(g1) = -12
FEATURE [PartDesign::Pocket] Pocket031
  BaseFeature = -> Pocket001
  Direction = (0,0,-1)
  Length = 5
  Length2 = 5
  Midplane = true
  Profile = -> Sketch070
  ReferenceAxis = -> Sketch070 [N_Axis]
  Suppressed = false
  Type = 1
FEATURE [Sketcher::SketchObject] Sketch118
  AttachmentSupport = -> [XZ_Plane015]
  FullyConstrained = true
  MapMode = 5
  Placement = pos=(0,0,0) rot=(1,0,0;1.5708rad)
  expr: Constraints[10] = <<pillar_base_sketch>>.Constraints.length / 2 - 2 mm
  expr: Constraints[9] = -<<pillar_bottom_BaseBend>>.length / 2
  sketch-geometry (11):
    g0: Circle CenterX=-43 CenterY=9 CenterZ=0 NormalX=0 NormalY=0 NormalZ=1 AngleXU=0 Radius=1.7
    g1: Circle CenterX=-43 CenterY=40.3333 CenterZ=0 NormalX=0 NormalY=0 NormalZ=1 AngleXU=0 Radius=1.7
    g2: Circle CenterX=-43 CenterY=103 CenterZ=0 NormalX=0 NormalY=0 NormalZ=1 AngleXU=0 Radius=1.7
    g3: LineSegment StartX=-43 StartY=9 StartZ=0 EndX=-43 EndY=40.3333 EndZ=0
    g4: GeomPoint X=-50.5 Y=0 Z=0
    g5: GeomPoint X=-43 Y=110 Z=0
    g6: LineSegment StartX=-43 StartY=103 StartZ=0 EndX=-43 EndY=110 EndZ=0
    g7: LineSegment StartX=-43 StartY=9 StartZ=0 EndX=-43 EndY=0 EndZ=0
    g8: LineSegment StartX=-43 StartY=40.3333 StartZ=0 EndX=-43 EndY=71.6667 EndZ=0
    g9: LineSegment StartX=-43 StartY=71.6667 StartZ=0 EndX=-43 EndY=103 EndZ=0
    g10: Circle CenterX=-43 CenterY=71.6667 CenterZ=0 NormalX=0 NormalY=0 NormalZ=1 AngleXU=0 Radius=1.7
  constraints (27):
    c: Equal(g0,g1)
    c: Equal(g0,g2)
    c: Diameter(g0) = 3.4
    c: Coincident(g3,g0)
    c: Coincident(g3,g1)
    c: Vertical(g3)
    c: Coincident(g8,g1)
    c: Coincident(g9,g2)
    c: PointOnObject(g4,g-1)
    c: DistanceX(g4) = -50.5
    c: DistanceX(g4,g0) = 7.5
    c: DistanceY(g5) = 110
    c: Coincident(g6,g2)
    c: Coincident(g6,g5)
    c: Vertical(g6)
    c: Coincident(g7,g0)
    c: PointOnObject(g7,g-1)
    c: Vertical(g7)
    c: DistanceY(g7,g7) = 9
    c: DistanceY(g6,g6) = 7
    c: Coincident(g8,g9)
    c: Vertical(g8)
    c: Vertical(g9)
    c: Equal(g3,g8)
    c: Equal(g8,g9)
    c: Coincident(g10,g8)
    c: Equal(g0,g10)
FEATURE [PartDesign::Pocket] Pocket063
  BaseFeature = -> Pocket031
  Direction = (0,1,-2e-16)
  Length = 5
  Length2 = 5
  Profile = -> Sketch118
  ReferenceAxis = -> Sketch118 [N_Axis]
  Reversed = true
  Suppressed = false
  Type = 0
FEATURE [PartDesign::CoordinateSystem] pillar_bottom_LCS
  AttacherType = Attacher::AttachEngine3D
  AttachmentOffset = pos=(-50.5,0,0) rot=(0,0,1;0rad)
  AttachmentSupport = -> [XY_Plane015]
  MapMode = 5
  Placement = pos=(-50.5,0,0) rot=(0,0,1;0rad)
FEATURE [PartDesign::Body] Body011  label="pillar_bottom_material_0.30ansi"
  Group = -> [Sketch010,BaseBend005,Sketch011,Sketch012,WireFilter,WireFilter001,Pocket,Pocket001,Sketch070,Pocket031,Sketch118,Pocket063,pillar_bottom_LCS]
  Origin = -> Origin015
  Placement = pos=(18.3,54.5,0) rot=(0,0,1;1.5708rad)
  Tip = -> Pocket063
  expr: Placement = <<pillar_bottom_placement>>.AttachmentOffset
COMPONENT P52 — recipe-attached ("pillar_material_0.30ansi001", modeled in this document).
Construction recipe (the document's own serialized feature program — sketch geometry with constraints, then the solid features built on it; lengths are millimeters unless a unit is written):

FEATURE [PartDesign::SubShapeBinder] Binder002
  BindCopyOnChange = 0
  BindMode = 0
  ClaimChildren = true
  Fuse = false
  MakeFace = true
  OffsetFill = false
  OffsetIntersection = false
  OffsetJoinType = 0
  OffsetOpenResult = false
  PartialLoad = false
  Relative = false
  Support = -> [Sketch008]
  _Version = 2
FEATURE [PartDesign::FeaturePython] BaseBend004  label="pillar_BaseBend"  # WARN: FeaturePython — macro-defined, semantics opaque (R4)
  BendSide = 1
  BendSketch = -> Binder002
  MidPlane = false
  Reverse = false
  Suppressed = false
  length = 1594
  radius = 2
  thickness = 2
FEATURE [Sketcher::SketchObject] Sketch009
  AttachmentOffset = pos=(0,1594,0) rot=(0,0,1;0rad)
  AttachmentSupport = -> [XZ_Plane014]
  FullyConstrained = true
  MapMode = 5
  Placement = pos=(0,3.539e-13,1594) rot=(1,0,0;1.5708rad)
  expr: .AttachmentOffset.Base.y = BaseBend004.length
  expr: Constraints[15] = <<pillar_base_sketch>>.Constraints.width - (<<pillar_BaseBend>>.thickness + <<pillar_BaseBend>>.radius) * 2
  sketch-geometry (16):
    g0: LineSegment StartX=-14.3 StartY=0 StartZ=0 EndX=14.3 EndY=0 EndZ=0
    g1: LineSegment StartX=14.3 StartY=0 StartZ=0 EndX=14.3 EndY=2 EndZ=0
    g2: LineSegment StartX=14.3 StartY=2 StartZ=0 EndX=34.5 EndY=2 EndZ=0
    g3: LineSegment StartX=37.5 StartY=5 StartZ=0 EndX=37.5 EndY=87 EndZ=0
    g4: LineSegment StartX=34.5 StartY=90 StartZ=0 EndX=-34.5 EndY=90 EndZ=0
    g5: LineSegment StartX=-37.5 StartY=87 StartZ=0 EndX=-37.5 EndY=5 EndZ=0
    g6: LineSegment StartX=-34.5 StartY=2 StartZ=0 EndX=-14.3 EndY=2 EndZ=0
    g7: LineSegment StartX=-14.3 StartY=2 StartZ=0 EndX=-14.3 EndY=0 EndZ=0
    g8: ArcOfCircle CenterX=34.5 CenterY=5 CenterZ=0 NormalX=0 NormalY=0 NormalZ=1 AngleXU=0 Radius=3 StartAngle=4.71239 EndAngle=6.28319
    g9: GeomPoint X=37.5 Y=2 Z=0
    g10: ArcOfCircle CenterX=34.5 CenterY=87 CenterZ=0 NormalX=0 NormalY=0 NormalZ=1 AngleXU=0 Radius=3 StartAngle=1.02861e-11 EndAngle=1.5708
    g11: GeomPoint X=37.5 Y=90 Z=0
    g12: ArcOfCircle CenterX=-34.5 CenterY=87 CenterZ=0 NormalX=0 NormalY=0 NormalZ=1 AngleXU=0 Radius=3 StartAngle=1.5708 EndAngle=3.14159
    g13: GeomPoint X=-37.5 Y=90 Z=0
    g14: ArcOfCircle CenterX=-34.5 CenterY=5 CenterZ=0 NormalX=0 NormalY=0 NormalZ=1 AngleXU=0 Radius=3 StartAngle=3.14159 EndAngle=4.71239
    g15: GeomPoint X=-37.5 Y=2 Z=0
  constraints (38):
    c: PointOnObject(g0,g-1)
    c: Coincident(g0,g1)
    c: Vertical(g1)
    c: Coincident(g1,g2)
    c: Horizontal(g2)
    c: Vertical(g3)
    c: Vertical(g5)
    c: Horizontal(g6)
    c: Coincident(g6,g7)
    c: Vertical(g7)
    c: Coincident(g0,g7)
    c: Horizontal(g0)
    c: Symmetric(g6,g1,g-2)
    c: Symmetric(g11,g13,g-2)
    c: DistanceY(g1,g1) = 2
    c: DistanceX(g0,g0) = 28.6
    c: PointOnObject(g9,g2)
    c: PointOnObject(g9,g3)
    c: Tangent(g2,g8) = -1.5708
    c: Tangent(g3,g8) = -1.5708
    c: PointOnObject(g11,g3)
    c: PointOnObject(g11,g4)
    c: Tangent(g3,g10) = -1.5708
    c: Tangent(g4,g10) = -1.5708
    c: PointOnObject(g13,g4)
    c: PointOnObject(g13,g5)
    c: Tangent(g4,g12) = -1.5708
    c: Tangent(g5,g12) = -1.5708
    c: PointOnObject(g15,g5)
    c: PointOnObject(g15,g6)
    c: Tangent(g5,g14) = -1.5708
    c: Tangent(g6,g14) = -1.5708
    c: Equal(g14,g8)
    c: Equal(g14,g10)
    c: Equal(g14,g12)
    c: Radius(g14) = 3
    c: DistanceX(g13,g11) = 75
    c: DistanceY(g9,g11) = 88
FEATURE [PartDesign::SubShapeBinder] Binder072
  BindCopyOnChange = 0
  BindMode = 0
  ClaimChildren = true
  Context = -> Body010 [Binder072.]
  Fuse = false
  MakeFace = true
  OffsetFill = false
  OffsetIntersection = false
  OffsetJoinType = 0
  OffsetOpenResult = false
  PartialLoad = false
  Relative = true
  Support = -> [Body011[Pocket063.Sketch118.]]
  _Version = 2
FEATURE [PartDesign::Fillet] Fillet002
  Base = -> BaseBend004 [Edge10,Edge39,Edge41,Edge8]
  BaseFeature = -> BaseBend004
  Radius = 5
  SupportTransform = false
  Suppressed = false
  UseAllEdges = false
FEATURE [PartDesign::Pad] Pad
  BaseFeature = -> Fillet002
  Direction = (0,-1,2e-16)
  Length = 2
  Length2 = 10
  Profile = -> Sketch009
  ReferenceAxis = -> Sketch009 [N_Axis]
  Reversed = true
  Suppressed = false
  Type = 0
  expr: Length = <<pillar_BaseBend>>.thickness
FEATURE [PartDesign::Boolean] Boolean011
  BaseFeature = -> Pad
  Group = -> [Compound030]
  Refine = true
  Suppressed = false
  Type = 1
  UsePlacement = false
  expr: Group = <<pillar_cut1>>._self
FEATURE [PartDesign::Hole] Hole019
  BaseFeature = -> Boolean011
  CustomThreadClearance = 0
  Depth = 3405.27
  DepthType = 1
  Diameter = 3.4
  DrillForDepth = false
  DrillPoint = 1
  DrillPointAngle = 118
  HoleCutCountersinkAngle = 90
  HoleCutCustomValues = false
  HoleCutDepth = 0
  HoleCutDiameter = 6.1
  HoleCutType = 0
  ModelThread = false
  Profile = -> Binder072
  Suppressed = false
  Tapered = false
  TaperedAngle = 90
  ThreadClass = 0
  ThreadDepth = 3405.27
  ThreadDepthType = 0
  ThreadDirection = 0
  ThreadFit = 0
  ThreadSize = 0
  ThreadType = 0
  Threaded = false
  UseCustomThreadClearance = false
  expr: Diameter = <<Properties>>.rivet_d
FEATURE [PartDesign::Body] Body010  label="pillar_material_0.30ansi"
  Group = -> [Binder002,BaseBend004,Sketch009,Fillet002,Pad,Boolean011,Binder072,Hole019]
  Origin = -> Origin014
  Tip = -> Hole019
COMPONENT P53 — recipe-attached ("pillar_top_element_material_0.30ansi001", modeled in this document).
Construction recipe (the document's own serialized feature program — sketch geometry with constraints, then the solid features built on it; lengths are millimeters unless a unit is written):

FEATURE [Sketcher::SketchObject] Sketch013
  AttachmentSupport = -> [XY_Plane016]
  FullyConstrained = true
  MapMode = 5
  sketch-geometry (5):
    g0: LineSegment StartX=-36 StartY=25 StartZ=0 EndX=-36 EndY=0 EndZ=0
    g1: LineSegment StartX=-36 StartY=0 StartZ=0 EndX=36 EndY=0 EndZ=0
    g2: LineSegment StartX=36 StartY=0 StartZ=0 EndX=36 EndY=25 EndZ=0
    g3: LineSegment StartX=36 StartY=25 StartZ=0 EndX=-36 EndY=25 EndZ=0
    g4: GeomPoint X=0 Y=12.5 Z=0
  constraints (13):
    c: Coincident(g0,g1)
    c: Coincident(g1,g2)
    c: Coincident(g2,g3)
    c: Coincident(g3,g0)
    c: Horizontal(g1)
    c: Horizontal(g3)
    c: Vertical(g0)
    c: Vertical(g2)
    c: Symmetric(g1,g0,g4)
    c: PointOnObject(g4,g-2)
    c: PointOnObject(g1,g-1)
    c: DistanceY(g2,g2) = 25
    c: DistanceX(g1,g1) = 72
FEATURE [PartDesign::FeaturePython] BaseBend006  # WARN: FeaturePython — macro-defined, semantics opaque (R4)
  BendSide = 1
  BendSketch = -> Sketch013
  MidPlane = false
  Reverse = false
  Suppressed = false
  length = 84
  radius = 2
  thickness = 2
FEATURE [PartDesign::FeaturePython] Bend  # WARN: FeaturePython — macro-defined, semantics opaque (R4)
  AutoMiter = true
  BaseFeature = -> BaseBend006
  BendType = 1
  LengthList = [70]
  LengthSpec = 1
  ReliefFactor = 0.7
  Suppressed = false
  UseReliefFactor = false
  angle = 90
  baseObject = -> BaseBend006 [Edge26]
  bendAList = [90]
  extend1 = 0
  extend2 = 0
  gap1 = 0
  gap2 = 0
  invert = false
  kfactor = 0.5
  length = 70
  maxExtendDist = 5
  minGap = 0.1
  minReliefGap = 1
  miterangle1 = 0
  miterangle2 = 0
  offset = 0
  radius = 2
  reliefType = 0
  reliefd = 1
  reliefw = 0.8
  sketchflip = false
  sketchinvert = false
  unfold = false
  expr: radius = BaseBend006.radius
FEATURE [Sketcher::SketchObject] Sketch066
  AttachmentSupport = -> [XY_Plane016]
  FullyConstrained = true
  MapMode = 5
  expr: Constraints[6] = <<Properties>>.rivet_d
  sketch-geometry (3):
    g0: Circle CenterX=0 CenterY=35 CenterZ=0 NormalX=0 NormalY=0 NormalZ=1 AngleXU=0 Radius=1.7
    g1: Circle CenterX=25 CenterY=60 CenterZ=0 NormalX=0 NormalY=0 NormalZ=1 AngleXU=0 Radius=1.7
    g2: Circle CenterX=-25 CenterY=60 CenterZ=0 NormalX=0 NormalY=0 NormalZ=1 AngleXU=0 Radius=1.7
  constraints (8):
    c: PointOnObject(g0,g-2)
    c: DistanceY(g0) = 35
    c: DistanceX(g1) = 25
    c: DistanceY(g1) = 60
    c: Equal(g0,g1)
    c: Equal(g0,g2)
    c: Diameter(g0) = 3.4
    c: Symmetric(g2,g1,g-2)
FEATURE [Sketcher::SketchObject] Sketch067
  AttachmentSupport = -> [XY_Plane016]
  FullyConstrained = true
  MapMode = 5
  sketch-geometry (13):
    g0: LineSegment StartX=-8.5 StartY=28 StartZ=0 EndX=-8.5 EndY=0 EndZ=0
    g1: LineSegment StartX=-8.5 StartY=0 StartZ=0 EndX=8.5 EndY=0 EndZ=0
    g2: LineSegment StartX=8.5 StartY=28 StartZ=0 EndX=-8.5 EndY=28 EndZ=0
    g3: GeomPoint X=0 Y=14 Z=0
    g4: LineSegment StartX=8.5 StartY=0 StartZ=0 EndX=14 EndY=0 EndZ=0
    g5: LineSegment StartX=8.5 StartY=20.9904 StartZ=0 EndX=8.5 EndY=28 EndZ=0
    g6: ArcOfCircle CenterX=8.5 CenterY=8 CenterZ=0 NormalX=0 NormalY=0 NormalZ=1 AngleXU=0 Radius=7.5 StartAngle=0 EndAngle=1.0472
    g7: ArcOfCircle CenterX=16 CenterY=20.9904 CenterZ=0 NormalX=0 NormalY=0 NormalZ=1 AngleXU=0 Radius=7.5 StartAngle=3.14159 EndAngle=4.18879
    g8: LineSegment StartX=14 StartY=0 StartZ=0 EndX=14 EndY=4 EndZ=0
    g9: LineSegment StartX=14 StartY=4 StartZ=0 EndX=14 EndY=10 EndZ=0
    g10: LineSegment StartX=16 StartY=6 StartZ=0 EndX=16 EndY=8 EndZ=0
    g11: ArcOfCircle CenterX=15 CenterY=4 CenterZ=0 NormalX=0 NormalY=0 NormalZ=1 AngleXU=0 Radius=1 StartAngle=1.5708 EndAngle=3.14159
    g12: ArcOfCircle CenterX=15 CenterY=6 CenterZ=0 NormalX=0 NormalY=0 NormalZ=1 AngleXU=0 Radius=1 StartAngle=4.71239 EndAngle=6.28319
  constraints (34):
    c: Coincident(g0,g1)
    c: Coincident(g1,g4)
    c: Coincident(g5,g2)
    c: Coincident(g2,g0)
    c: Horizontal(g1)
    c: Vertical(g0)
    c: Symmetric(g1,g0,g3)
    c: PointOnObject(g3,g-2)
    c: PointOnObject(g1,g-1)
    c: DistanceX(g2,g2) = 17
    c: DistanceY(g4,g5) = 28
    c: Coincident(g4,g8)
    c: Vertical(g5)
    c: Horizontal(g4)
    c: DistanceX(g4,g4) = 5.5
    c: DistanceY(g8,g9) = 10
    c: Symmetric(g2,g0,g-2)
    c: Tangent(g7,g6) = 1.5708
    c: Tangent(g7,g5) = 1.5708
    c: PointOnObject(g6,g5)
    c: Equal(g6,g7)
    c: Coincident(g8,g9)
    c: Vertical(g8)
    c: Vertical(g9)
    c: DistanceY(g8,g8) = 4
    c: Vertical(g10)
    c: DistanceX(g10) = 16
    c: Tangent(g11,g8) = 1.5708
    c: Tangent(g12,g11) = 1.5708
    c: Tangent(g12,g10) = -1.5708
    c: Equal(g12,g11)
    c: Tangent(g6,g10) = -1.5708
    c: Vertical(g11,g11)
    c: DistanceY(g10,g10) = 2
FEATURE [Sketcher::SketchObject] Sketch073
  AttachmentSupport = -> [YZ_Plane016]
  FullyConstrained = true
  MapMode = 5
  Placement = pos=(0,0,0) rot=(0.57735,0.57735,0.57735;2.0944rad)
  expr: Constraints[5] = <<Properties>>.rivet_d
  sketch-geometry (2):
    g0: Circle CenterX=10 CenterY=80 CenterZ=0 NormalX=0 NormalY=0 NormalZ=1 AngleXU=0 Radius=1.7
    g1: Circle CenterX=10 CenterY=10 CenterZ=0 NormalX=0 NormalY=0 NormalZ=1 AngleXU=0 Radius=1.7
  constraints (6):
    c: Vertical(g1,g0)
    c: DistanceX(g1) = 10
    c: DistanceY(g0) = 80
    c: DistanceY(g1) = 10
    c: Equal(g1,g0)
    c: Diameter(g1) = 3.4
FEATURE [PartDesign::Fillet] Fillet001
  Base = -> Bend [Edge65,Edge66,Edge8,Edge64,Edge50,Edge2]
  BaseFeature = -> Bend
  Radius = 5
  SupportTransform = false
  Suppressed = false
  UseAllEdges = false
FEATURE [PartDesign::Hole] Hole005
  BaseFeature = -> Fillet001
  CustomThreadClearance = 0
  Depth = 286.27
  DepthType = 1
  Diameter = 3.4
  DrillForDepth = false
  DrillPoint = 1
  DrillPointAngle = 118
  HoleCutCountersinkAngle = 90
  HoleCutCustomValues = false
  HoleCutDepth = 0
  HoleCutDiameter = 6.1
  HoleCutType = 0
  ModelThread = false
  Profile = -> Sketch066
  Reversed = true
  Suppressed = false
  Tapered = false
  TaperedAngle = 90
  ThreadClass = 0
  ThreadDepth = 286.27
  ThreadDepthType = 0
  ThreadDirection = 0
  ThreadFit = 0
  ThreadSize = 0
  ThreadType = 0
  Threaded = false
  UseCustomThreadClearance = false
  expr: Diameter = <<Properties>>.rivet_d
FEATURE [PartDesign::Pocket] Pocket030
  BaseFeature = -> Hole005
  Direction = (0,0,-1)
  Length = 5
  Length2 = 5
  Profile = -> Sketch067
  ReferenceAxis = -> Sketch067 [N_Axis]
  Reversed = true
  Suppressed = false
  Type = 0
FEATURE [PartDesign::Pocket] Pocket034
  BaseFeature = -> Pocket030
  Direction = (-1,0,0)
  Length = 5
  Length2 = 5
  Midplane = true
  Profile = -> Sketch073
  ReferenceAxis = -> Sketch073 [N_Axis]
  Suppressed = false
  Type = 1
FEATURE [PartDesign::SubShapeBinder] Binder074
  BindCopyOnChange = 0
  BindMode = 0
  ClaimChildren = false
  Context = -> Body012 [Binder074.]
  Fuse = false
  MakeFace = true
  OffsetFill = false
  OffsetIntersection = false
  OffsetJoinType = 0
  OffsetOpenResult = false
  PartialLoad = false
  Relative = true
  Support = -> [Body010[Boolean011.Edge138,Boolean011.Edge140,Boolean011.Edge152]]
  _Version = 2
FEATURE [PartDesign::Pocket] Pocket065
  BaseFeature = -> Pocket034
  Direction = (0,-1,2e-16)
  Length = 5
  Length2 = 5
  Profile = -> Binder074
  Reversed = true
  Suppressed = false
  Type = 0
FEATURE [PartDesign::Body] Body012  label="pillar_top_element_material_0.30ansi"
  Group = -> [Sketch013,BaseBend006,Bend,Sketch066,Fillet001,Hole005,Sketch067,Pocket030,Sketch073,Pocket034,Binder074,Pocket065]
  Origin = -> Origin016
  Placement = pos=(0,2,1594) rot=(0,0,1;0rad)
  Tip = -> Pocket065
COMPONENT P54 — recipe-attached ("led_holder_material_0.30ansi001", modeled in this document).
Construction recipe (the document's own serialized feature program — sketch geometry with constraints, then the solid features built on it; lengths are millimeters unless a unit is written):

FEATURE [PartDesign::SubShapeBinder] Binder034
  BindCopyOnChange = 0
  BindMode = 0
  ClaimChildren = true
  Fuse = false
  MakeFace = true
  OffsetFill = false
  OffsetIntersection = false
  OffsetJoinType = 0
  OffsetOpenResult = false
  PartialLoad = false
  Placement = pos=(0,0,1594) rot=(0,0,1;0rad)
  Relative = false
  Support = -> [Sketch055]
  _Version = 2
FEATURE [PartDesign::FeaturePython] BaseBend016  # WARN: FeaturePython — macro-defined, semantics opaque (R4)
  BendSide = 1
  BendSketch = -> Binder034
  MidPlane = false
  Reverse = true
  Suppressed = false
  length = 1122.3
  radius = 0.1
  thickness = 0.3
  expr: radius = composit_properties#<<Properties>>.bend_r
  expr: thickness = composit_properties#<<Properties>>.al_thickness
FEATURE [Sketcher::SketchObject] Sketch058
  AttachmentSupport = -> [XZ_Plane019]
  FullyConstrained = true
  MapMode = 5
  Placement = pos=(0,0,0) rot=(1,0,0;1.5708rad)
  sketch-geometry (5):
    g0: LineSegment StartX=8 StartY=497.7 StartZ=0 EndX=8 EndY=471.7 EndZ=0
    g1: LineSegment StartX=8 StartY=471.7 StartZ=0 EndX=-8 EndY=471.7 EndZ=0
    g2: LineSegment StartX=-8 StartY=471.7 StartZ=0 EndX=-8 EndY=497.7 EndZ=0
    g3: LineSegment StartX=-8 StartY=497.7 StartZ=0 EndX=8 EndY=497.7 EndZ=0
    g4: GeomPoint X=0 Y=484.7 Z=0
  constraints (13):
    c: Coincident(g0,g1)
    c: Coincident(g1,g2)
    c: Coincident(g2,g3)
    c: Coincident(g3,g0)
    c: Horizontal(g1)
    c: Horizontal(g3)
    c: Vertical(g0)
    c: Vertical(g2)
    c: Symmetric(g1,g0,g4)
    c: PointOnObject(g4,g-2)
    c: DistanceY(g0) = 471.7
    c: DistanceX(g1,g1) = 16
    c: DistanceY(g0,g0) = 26
FEATURE [PartDesign::Boolean] Boolean010
  BaseFeature = -> BaseBend016
  Group = -> [Compound031]
  Suppressed = false
  Type = 1
  UsePlacement = false
  expr: Group = <<led_holder_cut1>>._self
FEATURE [PartDesign::Pocket] Pocket028
  BaseFeature = -> Boolean010
  Direction = (0,1,-2e-16)
  Length = 5
  Length2 = 5
  Midplane = true
  Profile = -> Sketch058
  ReferenceAxis = -> Sketch058 [N_Axis]
  Suppressed = false
  Type = 1
FEATURE [PartDesign::Body] Body015  label="led_holder_material_0.30ansi"
  Group = -> [Binder034,BaseBend016,Boolean010,Sketch058,Pocket028]
  Origin = -> Origin019
  Tip = -> Pocket028
COMPONENT P55 — recipe-attached ("top_dec_corner_material_0.30ansi001", modeled in this document).
Construction recipe (the document's own serialized feature program — sketch geometry with constraints, then the solid features built on it; lengths are millimeters unless a unit is written):

FEATURE [Sketcher::SketchObject] Sketch119
  AttachmentSupport = -> [XY_Plane018]
  FullyConstrained = true
  MapMode = 5
  sketch-geometry (2):
    g0: LineSegment StartX=37.5 StartY=-1.5 StartZ=0 EndX=-37.5 EndY=-1.5 EndZ=0
    g1: LineSegment StartX=-37.5 StartY=-1.5 StartZ=0 EndX=-37.5 EndY=27 EndZ=0
  constraints (6):
    c: Coincident(g1,g0)
    c: Vertical(g1)
    c: DistanceY(g0) = -1.5
    c: Symmetric(g0,g0,g-2)
    c: DistanceX(g0,g0) = 75
    c: DistanceY(g1) = 27
FEATURE [PartDesign::FeaturePython] BaseBend029  # WARN: FeaturePython — macro-defined, semantics opaque (R4)
  BendSide = 1
  BendSketch = -> Sketch119
  MidPlane = false
  Placement = pos=(0,0,1588) rot=(0,0,1;0rad)
  Reverse = false
  Suppressed = false
  length = 96
  radius = 2
  thickness = 0.5
FEATURE [Sketcher::SketchObject] Sketch120
  AttachmentOffset = pos=(0,1588,0) rot=(0,0,1;0rad)
  AttachmentSupport = -> [XZ_Plane018]
  FullyConstrained = true
  MapMode = 5
  Placement = pos=(0,3.526e-13,1588) rot=(1,0,0;1.5708rad)
  expr: .AttachmentOffset.Base.y = BaseBend029.Placement.Base.z
  sketch-geometry (5):
    g0: ArcOfCircle CenterX=-35.5 CenterY=13.8267 CenterZ=0 NormalX=0 NormalY=0 NormalZ=1 AngleXU=0 Radius=13.8267 StartAngle=4.71239 EndAngle=5.38367
    g1: ArcOfCircle CenterX=-18.3 CenterY=-7.82667 CenterZ=0 NormalX=0 NormalY=0 NormalZ=1 AngleXU=0 Radius=13.8267 StartAngle=1.5708 EndAngle=2.24207
    g2: LineSegment StartX=-18.3 StartY=6 StartZ=0 EndX=40 EndY=6 EndZ=0
    g3: LineSegment StartX=40 StartY=6 StartZ=0 EndX=40 EndY=0 EndZ=0
    g4: LineSegment StartX=40 StartY=0 StartZ=0 EndX=-35.5 EndY=1.42e-14 EndZ=0
  constraints (15):
    c: PointOnObject(g0,g-1)
    c: Horizontal(g2)
    c: Coincident(g3,g2)
    c: PointOnObject(g3,g-1)
    c: Vertical(g3)
    c: Coincident(g4,g3)
    c: Coincident(g4,g0)
    c: Tangent(g4,g0)
    c: Equal(g0,g1)
    c: DistanceX(g0) = -35.5
    c: Tangent(g2,g1) = 1.5708
    c: Tangent(g1,g0) = 1.5708
    c: DistanceY(g3,g3) = 6
    c: DistanceX(g1) = -18.3
    c: DistanceX(g3) = 40
FEATURE [PartDesign::Pocket] Pocket064
  BaseFeature = -> BaseBend029
  Direction = (0,1,2e-16)
  Length = 5
  Length2 = 5
  Midplane = true
  Placement = pos=(0,0,1588) rot=(0,0,1;0rad)
  Profile = -> Sketch120
  ReferenceAxis = -> Sketch120 [N_Axis]
  Suppressed = false
  Type = 1
FEATURE [PartDesign::Fillet] Fillet004
  Base = -> Pocket064 [Edge25,Edge31,Edge8,Edge10]
  BaseFeature = -> Pocket064
  Placement = pos=(0,0,1588) rot=(0,0,1;0rad)
  Radius = 3
  SupportTransform = false
  Suppressed = false
  UseAllEdges = false
FEATURE [PartDesign::Boolean] Boolean014
  BaseFeature = -> Fillet004
  Group = -> [Compound044]
  Suppressed = false
  Type = 1
  UsePlacement = false
FEATURE [PartDesign::SubShapeBinder] Binder073
  BindCopyOnChange = 0
  BindMode = 0
  ClaimChildren = false
  Context = -> Link025 [Binder073.]
  Fuse = false
  MakeFace = true
  OffsetFill = false
  OffsetIntersection = false
  OffsetJoinType = 0
  OffsetOpenResult = false
  PartialLoad = false
  Relative = true
  Support = -> [Body012[Pocket034.Sketch073.]]
  _Version = 2
FEATURE [PartDesign::Hole] Hole020
  BaseFeature = -> Boolean014
  CustomThreadClearance = 0
  Depth = 253.566
  DepthType = 1
  Diameter = 3.4
  DrillForDepth = false
  DrillPoint = 1
  DrillPointAngle = 118
  HoleCutCountersinkAngle = 90
  HoleCutCustomValues = false
  HoleCutDepth = 0
  HoleCutDiameter = 6.1
  HoleCutType = 0
  ModelThread = false
  Profile = -> Binder073
  Suppressed = false
  Tapered = false
  TaperedAngle = 90
  ThreadClass = 0
  ThreadDepth = 253.566
  ThreadDepthType = 0
  ThreadDirection = 0
  ThreadFit = 0
  ThreadSize = 0
  ThreadType = 0
  Threaded = false
  UseCustomThreadClearance = false
  expr: Diameter = <<Properties>>.rivet_d
FEATURE [PartDesign::Body] Body014  label="top_dec_corner_material_0.30ansi"
  Group = -> [Sketch119,BaseBend029,Sketch120,Pocket064,Fillet004,Boolean014,Binder073,Hole020]
  Origin = -> Origin018
  Tip = -> Hole020
COMPONENT P56 — recipe-attached ("dec_corner_material_0.30ansi001", modeled in this document).
Construction recipe (the document's own serialized feature program — sketch geometry with constraints, then the solid features built on it; lengths are millimeters unless a unit is written):

FEATURE [PartDesign::SubShapeBinder] Binder035
  BindCopyOnChange = 0
  BindMode = 0
  ClaimChildren = true
  Fuse = false
  MakeFace = true
  OffsetFill = false
  OffsetIntersection = false
  OffsetJoinType = 0
  OffsetOpenResult = false
  PartialLoad = false
  Relative = false
  Support = -> [Sketch056]
  _Version = 2
FEATURE [PartDesign::FeaturePython] BaseBend017  # WARN: FeaturePython — macro-defined, semantics opaque (R4)
  BendSide = 0
  BendSketch = -> Binder035
  MidPlane = false
  Placement = pos=(0,0,481) rot=(0,0,1;0rad)
  Reverse = false
  Suppressed = false
  length = 1113
  radius = 2
  thickness = 0.5
FEATURE [PartDesign::Fillet] Fillet003
  Base = -> BaseBend017 [Edge23,Edge10,Edge25,Edge8]
  BaseFeature = -> BaseBend017
  Placement = pos=(0,0,481) rot=(0,0,1;0rad)
  Radius = 5
  SupportTransform = false
  Suppressed = false
  UseAllEdges = false
FEATURE [PartDesign::Boolean] Boolean012
  BaseFeature = -> Fillet003
  Group = -> [Compound032]
  Suppressed = false
  Type = 1
  UsePlacement = false
  expr: Group = <<dec_corner_cut1>>._self
FEATURE [PartDesign::Body] Body013  label="dec_corner_material_0.30ansi"
  Group = -> [Binder035,BaseBend017,Fillet003,Boolean012]
  Origin = -> Origin017
  Tip = -> Boolean012
COMPONENT P57 — recipe-attached ("basement_amplifier_material_0.30ansi002", modeled in this document).
Construction recipe (the document's own serialized feature program — sketch geometry with constraints, then the solid features built on it; lengths are millimeters unless a unit is written):

FEATURE [Sketcher::SketchObject] Sketch167  label="basement_amplifier_sketch"
  AttachmentSupport = -> [XY_Plane078]
  FullyConstrained = true
  MapMode = 5
  sketch-geometry (10):
    g0: LineSegment StartX=-25 StartY=320.166 StartZ=0 EndX=25 EndY=320.166 EndZ=0
    g1: LineSegment StartX=80 StartY=46.188 StartZ=0 EndX=0 EndY=0 EndZ=0
    g2: LineSegment StartX=0 StartY=0 StartZ=0 EndX=-80 EndY=46.188 EndZ=0
    g3: LineSegment StartX=25 StartY=320.166 StartZ=0 EndX=79.5375 EndY=48.492 EndZ=0
    g4: LineSegment StartX=79.5375 StartY=48.492 StartZ=0 EndX=80 EndY=46.188 EndZ=0
    g5: LineSegment StartX=-80 StartY=46.188 StartZ=0 EndX=-79.5375 EndY=48.492 EndZ=0
    g6: LineSegment StartX=-79.5375 StartY=48.492 StartZ=0 EndX=-25 EndY=320.166 EndZ=0
    g7: LineSegment StartX=-79.7343 StartY=47.5116 StartZ=0 EndX=-83.6561 EndY=48.2988 EndZ=0
    g8: LineSegment StartX=-83.6561 StartY=48.2988 StartZ=0 EndX=-81.0134 EndY=45.2961 EndZ=0
    g9: LineSegment StartX=-81.0134 StartY=45.2961 StartZ=0 EndX=-80 EndY=46.188 EndZ=0
  constraints (27):
    c: Coincident(g2,g5)
    c: Coincident(g6,g0)
    c: Coincident(g0,g3)
    c: Coincident(g4,g1)
    c: Symmetric(g1,g2,g-2)
    c: Symmetric(g0,g6,g-2)
    c: DistanceX(g0,g0) = 50
    c: DistanceY(g6) = 320.166  'length'
    c: DistanceX(g2,g1) = 160
    c: Coincident(g1,g2)
    c: Coincident(g3,g4)
    c: Symmetric(g5,g3,g-2)
    c: Coincident(g8,g7)
    c: Perpendicular(g5,g7)
    c: Equal(g8,g7)
    c: Distance(g7) = 4
    c: PointOnObject(g7,g5)
    c: Coincident(g6,g5)
    c: Distance(g7,g5) = 1
    c: Distance(g2) = 92.376  'inner_r'
    c: Angle(g1) = -2.61799
    c: Coincident(g9,g8)
    c: Coincident(g9,g2)
    c: Symmetric(g8,g7,g2)
    c: Parallel(g5,g6)
    c: Coincident(g1,g-1)
    c: Angle(g5,g9) = 2.49062  'connection_angle'
FEATURE [PartDesign::FeaturePython] BaseBend043  # WARN: FeaturePython — macro-defined, semantics opaque (R4)
  BendSide = 0
  BendSketch = -> Sketch167
  MidPlane = false
  Reverse = false
  Suppressed = false
  length = 100
  radius = 2
  thickness = 2
FEATURE [PartDesign::FeaturePython] Bend025  # WARN: FeaturePython — macro-defined, semantics opaque (R4)
  AutoMiter = false
  BaseFeature = -> BaseBend043
  BendType = 0
  LengthList = [100]
  LengthSpec = 0
  ReliefFactor = 0.7
  Suppressed = false
  UseReliefFactor = false
  angle = 90
  baseObject = -> BaseBend043 [Edge21,Edge7]
  bendAList = [90]
  extend1 = 0
  extend2 = 0
  gap1 = 0
  gap2 = 0
  invert = false
  kfactor = 0.5
  length = 100
  maxExtendDist = 5
  minGap = 0.1
  minReliefGap = 1
  miterangle1 = 18.649
  miterangle2 = 18.649
  offset = 0
  radius = 2
  reliefType = 0
  reliefd = 1
  reliefw = 0.8
  sketchflip = false
  sketchinvert = false
  unfold = false
  expr: miterangle1 = 90 deg - Sketch167.Constraints.connection_angle / 2
  expr: miterangle2 = miterangle1
  expr: radius = BaseBend043.radius
FEATURE [Sketcher::SketchObject] Sketch170
  AttachmentSupport = -> [YZ_Plane078]
  FullyConstrained = false
  MapMode = 5
  Placement = pos=(0,0,0) rot=(0.57735,0.57735,0.57735;2.0944rad)
  expr: Constraints[10] = <<basement_amplifier_sketch>>.Constraints.length
  sketch-geometry (11):
    g0: LineSegment StartX=320.166 StartY=-15 StartZ=0 EndX=320.166 EndY=2 EndZ=0
    g1: LineSegment StartX=320.166 StartY=2 StartZ=0 EndX=0 EndY=2 EndZ=0
    g2: LineSegment StartX=0 StartY=2 StartZ=0 EndX=0 EndY=-60 EndZ=0
    g3: LineSegment StartX=0 StartY=-60 StartZ=0 EndX=125.378 EndY=-25.2665 EndZ=0
    g4: LineSegment StartX=133.266 StartY=-24 StartZ=0 EndX=320.166 EndY=-15 EndZ=0
    g5: ArcOfCircle CenterX=135 CenterY=-60 CenterZ=0 NormalX=0 NormalY=0 NormalZ=1 AngleXU=0 Radius=36.0417 StartAngle=1.61891 EndAngle=1.84105
    g6: GeomPoint X=129.251 Y=-24.1933 Z=0
    g7: LineSegment StartX=-219.815 StartY=310.193 StartZ=0 EndX=564.966 EndY=310.193 EndZ=0
    g8: LineSegment StartX=564.966 StartY=310.193 StartZ=0 EndX=564.966 EndY=-309.063 EndZ=0
    g9: LineSegment StartX=564.966 StartY=-309.063 StartZ=0 EndX=-219.815 EndY=-309.063 EndZ=0
    g10: LineSegment StartX=-219.815 StartY=-309.063 StartZ=0 EndX=-219.815 EndY=310.193 EndZ=0
  constraints (27):
    c: Vertical(g0)
    c: Coincident(g0,g1)
    c: Horizontal(g1)
    c: PointOnObject(g2,g-2)
    c: Coincident(g4,g0)
    c: Coincident(g2,g1)
    c: Vertical(g2)
    c: DistanceY(g-1,g1) = 2
    c: DistanceY(g0,g1) = 17
    c: DistanceY(g2) = -60
    c: DistanceX(g1,g1) = 320.166
    c: PointOnObject(g6,g4)
    c: PointOnObject(g6,g3)
    c: Tangent(g4,g5) = 1.5708
    c: Tangent(g3,g5) = 1.5708
    c: Coincident(g7,g8)
    c: Coincident(g8,g9)
    c: Coincident(g9,g10)
    c: Coincident(g10,g7)
    c: Horizontal(g7)
    c: Horizontal(g9)
    c: Vertical(g8)
    c: Vertical(g10)
    c: DistanceY(g4) = -24
    c: DistanceX(g5) = 135
    c: Coincident(g3,g2)
    c: Horizontal(g5,g2)
FEATURE [PartDesign::Plane] DatumPlane005
  AttachmentOffset = pos=(0,0,0) rot=(0,-1,0;1.5708rad)
  AttachmentSupport = -> [Sketch167]
  Length = 647.453
  MapMode = 7
  Placement = pos=(-79.5375,48.492,0) rot=(0.501242,-0.611865,-0.611865;2.21231rad)
  ResizeMode = 0
  Width = 88.0953
FEATURE [PartDesign::Line] DatumLine003
  AttacherType = Attacher::AttachEngineLine
  AttachmentOffset = pos=(0,0,0) rot=(0,1,0;1.5708rad)
  AttachmentSupport = -> [Sketch170]
  Length = 20
  MapMode = 24
  Placement = pos=(0,0,-60) rot=(0,1,0;1.5708rad)
  ResizeMode = 0
FEATURE [PartDesign::Line] DatumLine004
  AttacherType = Attacher::AttachEngineLine
  AttachmentOffset = pos=(0,0,0) rot=(0,1,0;1.5708rad)
  AttachmentSupport = -> [Sketch170]
  Length = 20
  MapMode = 24
  Placement = pos=(0,133.266,-24) rot=(0.58639,0.558832,0.58639;2.1224rad)
  ResizeMode = 0
FEATURE [Sketcher::SketchObject] Sketch173
  AttachmentOffset = pos=(0,0,4) rot=(0,0,1;0rad)
  AttachmentSupport = -> [DatumPlane005]
  ExternalGeometry = -> [Sketch167]
  FullyConstrained = false
  MapMode = 5
  Placement = pos=(-83.4592,49.2793,0) rot=(-0.501242,0.611865,0.611865;4.07087rad)
  sketch-geometry (9):
    g0: LineSegment StartX=49.4595 StartY=-30.4174 StartZ=0 EndX=49.4595 EndY=2 EndZ=0
    g1: LineSegment StartX=-86.4657 StartY=-24 StartZ=0 EndX=-277.094 EndY=-15 EndZ=0
    g2: LineSegment StartX=-277.094 StartY=-15 StartZ=0 EndX=-277.094 EndY=2 EndZ=0
    g3: LineSegment StartX=-277.094 StartY=2 StartZ=0 EndX=49.4595 EndY=2 EndZ=0
    g4: LineSegment StartX=-568.045 StartY=-343.581 StartZ=0 EndX=236.236 EndY=-343.581 EndZ=0
    g5: LineSegment StartX=236.236 StartY=-343.581 StartZ=0 EndX=236.236 EndY=220.397 EndZ=0
    g6: LineSegment StartX=236.236 StartY=220.397 StartZ=0 EndX=-568.045 EndY=220.397 EndZ=0
    g7: LineSegment StartX=-568.045 StartY=220.397 StartZ=0 EndX=-568.045 EndY=-343.581 EndZ=0
    g8: LineSegment StartX=-86.4657 StartY=-24 StartZ=0 EndX=49.4595 EndY=-30.4174 EndZ=0
  constraints (22):
    c: Coincident(g2,g1)
    c: Vertical(g2)
    c: Coincident(g3,g2)
    c: Horizontal(g3)
    c: Coincident(g3,g0)
    c: DistanceY(g0) = 2
    c: DistanceY(g1) = -15
    c: Coincident(g4,g5)
    c: Coincident(g5,g6)
    c: Coincident(g6,g7)
    c: Coincident(g7,g4)
    c: Horizontal(g4)
    c: Horizontal(g6)
    c: Vertical(g5)
    c: Vertical(g7)
    c: PointOnObject(g-5,g2)
    c: Coincident(g1,g-4) = -1.5708
    c: Coincident(g8,g1)
    c: Coincident(g8,g0)
    c: Parallel(g8,g1)
    c: Vertical(g0)
    c: PointOnObject(g-3,g0)
FEATURE [PartDesign::Pocket] Pocket104
  BaseFeature = -> Bend025
  Direction = (0.98044,-0.19682,0)
  Length = 2
  Length2 = 5
  Profile = -> Sketch173
  ReferenceAxis = -> Sketch173 [N_Axis]
  Suppressed = false
  Type = 0
FEATURE [PartDesign::Fillet] Fillet011
  Base = -> Pocket104 [Edge57,Edge56]
  BaseFeature = -> Pocket104
  Radius = 10
  SupportTransform = false
  Suppressed = false
  UseAllEdges = false
FEATURE [PartDesign::SubShapeBinder] Binder118
  BindCopyOnChange = 0
  BindMode = 0
  ClaimChildren = false
  Context = -> Body105 [Binder118.]
  Fuse = false
  MakeFace = true
  OffsetFill = false
  OffsetIntersection = false
  OffsetJoinType = 0
  OffsetOpenResult = false
  PartialLoad = false
  Relative = true
  Support = -> [Body006[Binder069.]]
  _Version = 2
FEATURE [PartDesign::SubShapeBinder] Binder119
  BindCopyOnChange = 0
  BindMode = 0
  ClaimChildren = false
  Context = -> Body105 [Binder119.]
  Fuse = false
  MakeFace = true
  OffsetFill = false
  OffsetIntersection = false
  OffsetJoinType = 0
  OffsetOpenResult = false
  PartialLoad = false
  Relative = true
  Support = -> [Body006[Pocket061.Sketch112.]]
  _Version = 2
FEATURE [PartDesign::Pocket] Pocket108
  BaseFeature = -> Fillet011
  Direction = (0,0,-1)
  Length = 5
  Length2 = 5
  Midplane = true
  Profile = -> Binder119
  Suppressed = false
  Type = 1
FEATURE [Sketcher::SketchObject] Sketch175
  AttachmentSupport = -> [XY_Plane078]
  ExternalGeometry = -> [Sketch167]
  FullyConstrained = true
  MapMode = 5
  sketch-geometry (6):
    g0: Circle CenterX=43.3161 CenterY=155 CenterZ=0 NormalX=0 NormalY=0 NormalZ=1 AngleXU=0 Radius=2.55
    g1: Circle CenterX=-43.3161 CenterY=155 CenterZ=0 NormalX=0 NormalY=0 NormalZ=1 AngleXU=0 Radius=2.55
    g2: Circle CenterX=63.3907 CenterY=55 CenterZ=0 NormalX=0 NormalY=0 NormalZ=1 AngleXU=0 Radius=2.55
    g3: Circle CenterX=-63.3907 CenterY=55 CenterZ=0 NormalX=0 NormalY=0 NormalZ=1 AngleXU=0 Radius=2.55
    g4: LineSegment StartX=45.8162 StartY=155.502 StartZ=0 EndX=57.5815 EndY=157.864 EndZ=0
    g5: LineSegment StartX=65.8909 StartY=55.5019 StartZ=0 EndX=77.6561 EndY=57.8637 EndZ=0
  constraints (18):
    c: Distance(g0,g-3) = 12
    c: Diameter(g0) = 5.1
    c: Equal(g1,g0)
    c: Symmetric(g1,g0,g-2)
    c: DistanceY(g0) = 155
    c: Symmetric(g2,g3,g-2)
    c: Equal(g2,g3)
    c: Equal(g3,g0)
    c: PointOnObject(g4,g0)
    c: PointOnObject(g4,g-3)
    c: PointOnObject(g5,g2)
    c: PointOnObject(g5,g-3)
    c: Perpendicular(g5,g-3)
    c: PointOnObject(g2,g5)
    c: Equal(g5,g4)
    c: PointOnObject(g0,g4)
    c: Perpendicular(g-3,g4)
    c: DistanceY(g2) = 55
FEATURE [PartDesign::Pocket] Pocket109
  BaseFeature = -> Pocket108
  Direction = (0,0,-1)
  Length = 5
  Length2 = 5
  Midplane = true
  Profile = -> Sketch175
  ReferenceAxis = -> Sketch175 [N_Axis]
  Suppressed = false
  Type = 1
FEATURE [PartDesign::Mirrored] Mirrored010
  BaseFeature = -> Pocket109
  MirrorPlane = -> YZ_Plane078
  Originals = -> [Pocket104,Fillet011]
  Suppressed = false
FEATURE [PartDesign::FeatureAdditivePython] PDW_Common_Add  # link proxy (typed FeaturePython)
  BaseFeature = -> Mirrored010
  Body = Body105
  ClaimChildren = false
  EditPlacementAdjustments = false
  Enabled = 0
  LinkedObject = -> Mirrored010
  MeshTolerance = 0.1
  PatternBase = -> Pocket109
  PatternBaseOffset = 0
  PatternBaseScale = 1
  PatternBaseScaleXYZ = (1,1,1)
  PatternOffsetCut = false
  PatternOffsetIntersection = false
  PatternOffsetJoin = 0
  PatternOffsetMode = 0
  PatternOffsetSelfIntersection = false
  PatternOperation = 3
  PatternOperationDefault = Common
  PatternScaleCut = false
  PatternShapeOffset = 0
  PatternShapeScale = 1
  PatternShapeScaleXYZ = (1,1,1)
  PatternTool = -> Mirrored010
  PatternToolOffset = 0
  PatternToolScale = 1
  PatternToolScaleXYZ = (1,1,1)
  RefineMesh = true
  ShapeManagement = 0
  ShowMeshProps = false
  ShowOffsetProps = false
  ShowScaleProps = false
  ShowWarnings = true
  Suppressed = false
  TipBase = -> Mirrored010
  TipBaseOffset = 0
  TipBaseScale = 1
  TipBaseScaleXYZ = (1,1,1)
  TipOffsetCut = false
  TipOffsetIntersection = false
  TipOffsetJoin = 0
  TipOffsetMode = 0
  TipOffsetSelfIntersection = false
  TipOperation = 4
  TipOperationDefault = Common
  TipScaleCut = false
  TipShapeOffset = 0
  TipShapeScale = 1
  TipShapeScaleXYZ = (1,1,1)
  TipTool = -> Mirrored010
  TipToolOffset = 0
  TipToolScale = 1
  TipToolScaleXYZ = (1,1,1)
  Type = Additive
  UsePatternBaseAddSubShape = false
  UsePatternToolAddSubShape = true
  UseTipBaseAddSubShape = false
  UseTipToolAddSubShape = true
  Version = 0.2023.08.13
FEATURE [PartDesign::PolarPattern] PolarPattern006
  Angle = 360
  Axis = -> Z_Axis078
  BaseFeature = -> PDW_Common_Add
  Mode = 0
  Occurrences = 3
  Offset = 120
  Originals = -> [PDW_Common_Add]
  Refine = true
  Suppressed = false
FEATURE [PartDesign::Pocket] Pocket107
  BaseFeature = -> PolarPattern006
  Direction = (0,0,-1)
  Length = 5
  Length2 = 5
  Midplane = true
  Profile = -> Binder118
  Suppressed = false
  Type = 1
FEATURE [PartDesign::Boolean] Boolean028
  BaseFeature = -> Pocket107
  Group = -> [Compound070]
  Suppressed = false
  Type = 1
  UsePlacement = false
FEATURE [PartDesign::CoordinateSystem] Local_CS021  label="basement_top_amplifier_bottom_LCS"
  AttacherType = Attacher::AttachEngine3D
  AttachmentSupport = -> [XY_Plane078]
  MapMode = 5
FEATURE [PartDesign::CoordinateSystem] Local_CS022  label="basement_top_amplifier_top_LCS"
  AttacherType = Attacher::AttachEngine3D
  AttachmentOffset = pos=(0,0,2) rot=(0,0,1;0rad)
  AttachmentSupport = -> [XY_Plane078]
  MapMode = 5
  Placement = pos=(0,0,2) rot=(0,0,1;0rad)
FEATURE [PartDesign::Body] Body105  label="basement_top_amplifier_material_0.50ansi"
  Group = -> [Sketch167,BaseBend043,Bend025,Pocket104,Fillet011,Binder119,Sketch170,DatumPlane005,DatumLine003,DatumLine004,Sketch173,Pocket108,Sketch175,Pocket109,Mirrored010,PDW_Common_Add,PolarPattern006,Binder118,Pocket107,Boolean028,Local_CS021,Local_CS022]
  Origin = -> Origin078
  Tip = -> Boolean028
COMPONENT P58 — recipe-attached ("basement_proxy001", modeled in this document).
Construction recipe (the document's own serialized feature program — sketch geometry with constraints, then the solid features built on it; lengths are millimeters unless a unit is written):

FEATURE [PartDesign::SubShapeBinder] Binder006
  BindCopyOnChange = 0
  BindMode = 0
  ClaimChildren = true
  Context = -> Body008 [Binder006.]
  Fuse = false
  MakeFace = true
  Offset = 2
  OffsetFill = false
  OffsetIntersection = false
  OffsetJoinType = 0
  OffsetOpenResult = false
  PartialLoad = false
  Relative = false
  Support = -> [Array003]
  _Version = 2
FEATURE [PartDesign::Pad] Pad003
  Direction = (0,0,1)
  Length = 3
  Length2 = 10
  Profile = -> Binder006
  Suppressed = false
  Type = 0
FEATURE [PartDesign::SubShapeBinder] Binder129
  BindCopyOnChange = 0
  BindMode = 0
  ClaimChildren = false
  Context = -> Link028 [Binder129.]
  Fuse = false
  MakeFace = true
  OffsetFill = false
  OffsetIntersection = false
  OffsetJoinType = 0
  OffsetOpenResult = false
  PartialLoad = false
  Relative = true
  Support = -> [Link005[Hole.Binder001.]]
  _Version = 2
FEATURE [PartDesign::Boolean] Boolean021
  BaseFeature = -> Pad003
  Group = -> [Compound063]
  Suppressed = false
  Type = 1
  UsePlacement = false
FEATURE [PartDesign::CoordinateSystem] Local_CS017  label="basement_top_proxy_bottom_LCS"
  AttacherType = Attacher::AttachEngine3D
  AttachmentSupport = -> [XY_Plane012]
  MapMode = 5
FEATURE [PartDesign::CoordinateSystem] Local_CS018  label="basement_top_proxy_top_LCS"
  AttacherType = Attacher::AttachEngine3D
  AttachmentOffset = pos=(0,0,3) rot=(0,0,1;0rad)
  AttachmentSupport = -> [XY_Plane012]
  MapMode = 5
  Placement = pos=(0,0,3) rot=(0,0,1;0rad)
FEATURE [PartDesign::Body] Body008  label="basement_top_proxy"
  Group = -> [Binder006,Pad003,Boolean021,Binder129,Local_CS017,Local_CS018]
  Origin = -> Origin012
  Placement = pos=(0,0,18) rot=(0,0,1;0rad)
  Tip = -> Boolean021
COMPONENT P59 — recipe-attached ("basement_plywood001", modeled in this document).
Construction recipe (the document's own serialized feature program — sketch geometry with constraints, then the solid features built on it; lengths are millimeters unless a unit is written):

FEATURE [PartDesign::SubShapeBinder] Binder005
  BindCopyOnChange = 0
  BindMode = 0
  ClaimChildren = true
  Context = -> Body006 [Binder005.]
  Fuse = false
  MakeFace = true
  OffsetFill = false
  OffsetIntersection = false
  OffsetJoinType = 0
  OffsetOpenResult = false
  PartialLoad = false
  Relative = false
  Support = -> [Array003]
  _Version = 2
FEATURE [PartDesign::Pad] Pad001
  Direction = (0,0,1)
  Length = 18
  Length2 = 10
  Profile = -> Binder005
  Refine = true
  Suppressed = false
  Type = 0
FEATURE [Sketcher::SketchObject] Sketch112
  AttachmentSupport = -> [XY_Plane010]
  FullyConstrained = true
  MapMode = 5
  sketch-geometry (2):
    g0: Circle CenterX=0 CenterY=311.872 CenterZ=0 NormalX=0 NormalY=0 NormalZ=1 AngleXU=0 Radius=2.75
    g1: Circle CenterX=0 CenterY=276.872 CenterZ=0 NormalX=0 NormalY=0 NormalZ=1 AngleXU=0 Radius=2.75
  constraints (6):
    c: PointOnObject(g0,g-2)
    c: PointOnObject(g1,g-2)
    c: Equal(g1,g0)
    c: Diameter(g1) = 5.5
    c: DistanceY(g1,g0) = 35
    c: DistanceY(g1) = 276.872
FEATURE [Sketcher::SketchObject] Sketch113
  AttachmentSupport = -> [XY_Plane010]
  FullyConstrained = true
  MapMode = 5
  sketch-geometry (9):
    g0: LineSegment StartX=-22.5 StartY=-136 StartZ=0 EndX=-22.5 EndY=-161 EndZ=0
    g1: LineSegment StartX=-22.5 StartY=-161 StartZ=0 EndX=22.5 EndY=-161 EndZ=0
    g2: LineSegment StartX=22.5 StartY=-161 StartZ=0 EndX=22.5 EndY=-136 EndZ=0
    g3: LineSegment StartX=22.5 StartY=-136 StartZ=0 EndX=-22.5 EndY=-136 EndZ=0
    g4: GeomPoint X=0 Y=-148.5 Z=0
    g5: Circle CenterX=22.5 CenterY=-161 CenterZ=0 NormalX=0 NormalY=0 NormalZ=1 AngleXU=0 Radius=2.75
    g6: Circle CenterX=22.5 CenterY=-136 CenterZ=0 NormalX=0 NormalY=0 NormalZ=1 AngleXU=0 Radius=2.75
    g7: Circle CenterX=-22.5 CenterY=-136 CenterZ=0 NormalX=0 NormalY=0 NormalZ=1 AngleXU=0 Radius=2.75
    g8: Circle CenterX=-22.5 CenterY=-161 CenterZ=0 NormalX=0 NormalY=0 NormalZ=1 AngleXU=0 Radius=2.75
  constraints (21):
    c: Coincident(g0,g1)
    c: Coincident(g1,g2)
    c: Coincident(g2,g3)
    c: Coincident(g3,g0)
    c: Horizontal(g1)
    c: Horizontal(g3)
    c: Vertical(g0)
    c: Vertical(g2)
    c: Symmetric(g1,g0,g4)
    c: PointOnObject(g4,g-2)
    c: Coincident(g5,g1)
    c: Coincident(g6,g2)
    c: Coincident(g7,g0)
    c: Coincident(g8,g0)
    c: Equal(g5,g8)
    c: Equal(g5,g7)
    c: Equal(g5,g6)
    c: Diameter(g5) = 5.5
    c: DistanceY(g2,g2) = 25
    c: DistanceX(g1,g1) = 45
    c: DistanceY(g6) = -136
FEATURE [Sketcher::SketchObject] Sketch166
  AttachmentOffset = pos=(349.171,0,0) rot=(0,0,1;0rad)
  AttachmentSupport = -> [YZ_Plane010]
  FullyConstrained = true
  MapMode = 5
  Placement = pos=(0,349.171,0) rot=(0.57735,0.57735,0.57735;2.0944rad)
  expr: .AttachmentOffset.Base.x = <<basement_sketch>>.Constraints.max_r
  sketch-geometry (3):
    g0: LineSegment StartX=-15 StartY=0 StartZ=0 EndX=0 EndY=15 EndZ=0
    g1: LineSegment StartX=0 StartY=15 StartZ=0 EndX=0 EndY=0 EndZ=0
    g2: LineSegment StartX=0 StartY=0 StartZ=0 EndX=-15 EndY=0 EndZ=0
  constraints (8):
    c: PointOnObject(g0,g-1)
    c: PointOnObject(g0,g-2)
    c: Coincident(g0,g1)
    c: Coincident(g1,g-1)
    c: Coincident(g1,g2)
    c: Coincident(g2,g0)
    c: Equal(g2,g1)
    c: DistanceY(g1,g1) = 15
FEATURE [Sketcher::SketchObject] Sketch216
  AttachmentOffset = pos=(350,0,0) rot=(0,0,1;0rad)
  AttachmentSupport = -> [YZ_Plane010]
  FullyConstrained = true
  MapMode = 5
  Placement = pos=(0,350,0) rot=(0.57735,0.57735,0.57735;2.0944rad)
  sketch-geometry (3):
    g0: LineSegment StartX=0 StartY=15 StartZ=0 EndX=-15 EndY=0 EndZ=0
    g1: LineSegment StartX=-15 StartY=0 StartZ=0 EndX=0 EndY=0 EndZ=0
    g2: LineSegment StartX=0 StartY=15 StartZ=0 EndX=0 EndY=0 EndZ=0
  constraints (8):
    c: PointOnObject(g0,g-2)
    c: PointOnObject(g0,g-1)
    c: Coincident(g0,g1)
    c: Coincident(g1,g-1)
    c: Coincident(g2,g0)
    c: Coincident(g2,g1)
    c: Equal(g1,g2)
    c: DistanceY(g2,g2) = 15
FEATURE [PartDesign::SubtractivePipe] SubtractivePipe
  AuxilleryCurvelinear = true
  AuxillerySpineTangent = false
  BaseFeature = -> Pad001
  Binormal = (0,0,0)
  Mode = 0
  Profile = -> Sketch216
  Spine = -> Binder005 [Edge1,Edge2,Edge3,Edge4,Edge5,Edge6,Edge7,Edge8,Edge9,Edge10,Edge11,Edge12,Edge13,Edge14,Edge15,Edge16,Edge17,Edge18]
  SpineTangent = false
  Suppressed = false
  Transformation = 0
  Transition = 0
FEATURE [PartDesign::Pocket] Pocket062
  BaseFeature = -> SubtractivePipe
  Direction = (0,0,-1)
  Length = 5
  Length2 = 5
  Midplane = true
  Profile = -> Sketch113
  ReferenceAxis = -> Sketch113 [N_Axis]
  Suppressed = false
  Type = 1
FEATURE [PartDesign::CoordinateSystem] Local_CS019  label="basement_top_plywood_bottom_LCS"
  AttacherType = Attacher::AttachEngine3D
  AttachmentSupport = -> [XY_Plane010]
  MapMode = 5
FEATURE [PartDesign::CoordinateSystem] Local_CS020  label="basement_top_plywood_top_LCS"
  AttacherType = Attacher::AttachEngine3D
  AttachmentOffset = pos=(0,0,18) rot=(0,0,1;0rad)
  AttachmentSupport = -> [XY_Plane010]
  MapMode = 5
  Placement = pos=(0,0,18) rot=(0,0,1;0rad)
FEATURE [PartDesign::Boolean] Boolean023
  BaseFeature = -> Pocket062
  Group = -> [Compound066]
  Refine = true
  Suppressed = false
  Type = 1
  UsePlacement = false
FEATURE [PartDesign::Body] Body006  label="basement_top_plywood"
  Group = -> [Binder005,Pad001,Sketch112,Sketch113,SubtractivePipe,Pocket062,Sketch166,Sketch216,Boolean023,Local_CS019,Local_CS020]
  Origin = -> Origin010
  Tip = -> Boolean023
COMPONENT P60 — recipe-attached ("basement2_amplifier_material_stainlessSteel001", modeled in this document).
Construction recipe (the document's own serialized feature program — sketch geometry with constraints, then the solid features built on it; lengths are millimeters unless a unit is written):

FEATURE [Sketcher::SketchObject] Sketch171  label="basement2_sketch"
  AttachmentSupport = -> [XY_Plane080]
  FullyConstrained = true
  MapMode = 5
  sketch-geometry (10):
    g0: LineSegment StartX=-80 StartY=46.188 StartZ=0 EndX=2.84e-14 EndY=-4.97e-14 EndZ=0
    g1: LineSegment StartX=2.84e-14 StartY=-4.97e-14 StartZ=0 EndX=80 EndY=46.188 EndZ=0
    g2: LineSegment StartX=80 StartY=46.188 StartZ=0 EndX=79.7011 EndY=48.0916 EndZ=0
    g3: LineSegment StartX=79.7011 StartY=48.0916 StartZ=0 EndX=42.5 EndY=285 EndZ=0
    g4: LineSegment StartX=42.5 StartY=285 StartZ=0 EndX=-42.5 EndY=285 EndZ=0
    g5: LineSegment StartX=-42.5 StartY=285 StartZ=0 EndX=-79.7011 EndY=48.0916 EndZ=0
    g6: LineSegment StartX=-79.7011 StartY=48.0916 StartZ=0 EndX=-80 EndY=46.188 EndZ=0
    g7: LineSegment StartX=80 StartY=46.188 StartZ=0 EndX=81.4991 EndY=44.9774 EndZ=0
    g8: LineSegment StartX=81.4991 StartY=44.9774 StartZ=0 EndX=84.6406 EndY=48.8672 EndZ=0
    g9: LineSegment StartX=84.6406 StartY=48.8672 StartZ=0 EndX=79.7011 EndY=48.0916 EndZ=0
  constraints (26):
    c: Coincident(g0,g-1)
    c: Coincident(g0,g1)
    c: Coincident(g1,g2)
    c: Coincident(g2,g3)
    c: Coincident(g3,g4)
    c: Coincident(g4,g5)
    c: Coincident(g5,g6)
    c: Coincident(g6,g0)
    c: Symmetric(g0,g1,g-2)
    c: Symmetric(g4,g3,g-2)
    c: Symmetric(g5,g2,g-2)
    c: Parallel(g2,g3)
    c: Angle(g1) = 0.523599
    c: Coincident(g7,g1)
    c: Symmetric(g7,g2,g1)
    c: DistanceX(g4,g4) = 85
    c: DistanceY(g3) = 285
    c: Coincident(g8,g7)
    c: Coincident(g9,g8)
    c: Coincident(g9,g2)
    c: Perpendicular(g2,g9)
    c: Perpendicular(g7,g8)
    c: Distance(g9) = 5
    c: Distance(g1) = 92.376  'inner_r'
    c: Angle(g7,g2) = 2.40591  'connection_angle'
    c: DistanceX(g0,g1) = 160
FEATURE [PartDesign::FeaturePython] BaseBend044  # WARN: FeaturePython — macro-defined, semantics opaque (R4)
  BendSide = 0
  BendSketch = -> Sketch171
  MidPlane = false
  Reverse = false
  Suppressed = false
  length = 100
  radius = 2
  thickness = 2
FEATURE [PartDesign::FeaturePython] Bend026  # WARN: FeaturePython — macro-defined, semantics opaque (R4)
  AutoMiter = false
  BaseFeature = -> BaseBend044
  BendType = 0
  LengthList = [30]
  LengthSpec = 0
  ReliefFactor = 0.7
  Suppressed = false
  UseReliefFactor = false
  angle = 90
  baseObject = -> BaseBend044 [Edge19,Edge13]
  bendAList = [90]
  extend1 = 0
  extend2 = 0
  gap1 = 0
  gap2 = 0
  invert = false
  kfactor = 0.5
  length = 30
  maxExtendDist = 5
  minGap = 0.1
  minReliefGap = 1
  miterangle1 = 21.0759
  miterangle2 = 21.0759
  offset = 0
  radius = 2
  reliefType = 0
  reliefd = 1
  reliefw = 0.8
  sketchflip = false
  sketchinvert = false
  unfold = false
  expr: miterangle1 = 90 deg - <<basement2_sketch>>.Constraints.connection_angle / 2
  expr: miterangle2 = miterangle1
  expr: radius = BaseBend044.radius
FEATURE [Sketcher::SketchObject] Sketch174
  AttachmentSupport = -> [XY_Plane080]
  ExternalGeometry = -> [Sketch171]
  FullyConstrained = true
  MapMode = 5
  sketch-geometry (7):
    g0: LineSegment StartX=44.3713 StartY=273.083 StartZ=0 EndX=49.3108 EndY=273.858 EndZ=0
    g1: LineSegment StartX=49.3108 StartY=273.858 StartZ=0 EndX=4.93947 EndY=556.429 EndZ=0
    g2: LineSegment StartX=4.93947 StartY=556.429 StartZ=0 EndX=0 EndY=555.654 EndZ=0
    g3: LineSegment StartX=42.5 StartY=285 StartZ=0 EndX=38.2239 EndY=285 EndZ=0
    g4: LineSegment StartX=43.1633 StartY=280.776 StartZ=0 EndX=44.3713 EndY=273.083 EndZ=0
    g5: LineSegment StartX=0 StartY=555.654 StartZ=0 EndX=42.5 EndY=285 EndZ=0
    g6: ArcOfCircle CenterX=38.2239 CenterY=280 CenterZ=0 NormalX=0 NormalY=0 NormalZ=1 AngleXU=0 Radius=5 StartAngle=0.155755 EndAngle=1.5708
  constraints (20):
    c: Coincident(g0,g1)
    c: Coincident(g1,g2)
    c: Coincident(g2,g5)
    c: Coincident(g4,g0)
    c: Parallel(g0,g2)
    c: Perpendicular(g1,g0)
    c: PointOnObject(g0,g-3)
    c: PointOnObject(g2,g-3)
    c: DistanceY(g0) = 273.083
    c: PointOnObject(g2,g-2)
    c: Distance(g0) = 5
    c: Coincident(g3,g-3)
    c: Horizontal(g3)
    c: Parallel(g1,g4)
    c: Parallel(g1,g5)
    c: Coincident(g5,g3)
    c: Tangent(g6,g4) = 1.5708
    c: Tangent(g6,g3) = -1.5708
    c: Radius(g6) = 5
    c: Distance(g3,g0) = 12.0632
FEATURE [PartDesign::Pocket] Pocket105
  BaseFeature = -> Bend026
  Direction = (0,0,-1)
  Length = 5
  Length2 = 5
  Midplane = true
  Profile = -> Sketch174
  ReferenceAxis = -> Sketch174 [N_Axis]
  Suppressed = false
  Type = 1
FEATURE [PartDesign::Mirrored] Mirrored011
  BaseFeature = -> Pocket105
  MirrorPlane = -> Sketch174 [V_Axis]
  Originals = -> [Pocket105]
  Refine = true
  Suppressed = false
FEATURE [PartDesign::SubShapeBinder] Binder117
  BindCopyOnChange = 0
  BindMode = 0
  ClaimChildren = false
  Context = -> Body107 [Binder117.]
  Fuse = false
  MakeFace = true
  OffsetFill = false
  OffsetIntersection = false
  OffsetJoinType = 0
  OffsetOpenResult = false
  PartialLoad = false
  Relative = true
  Support = -> [Body007[Binder066.Binder064.]]
  _Version = 2
FEATURE [Sketcher::SketchObject] Sketch176
  AttachmentSupport = -> [XY_Plane080]
  ExternalGeometry = -> [Sketch171]
  FullyConstrained = true
  MapMode = 5
  sketch-geometry (5):
    g0: LineSegment StartX=42.5 StartY=285 StartZ=0 EndX=42.5 EndY=362 EndZ=0
    g1: ArcOfCircle CenterX=27.5 CenterY=362 CenterZ=0 NormalX=0 NormalY=0 NormalZ=1 AngleXU=0 Radius=15 StartAngle=-8.4623e-11 EndAngle=1.5708
    g2: LineSegment StartX=0 StartY=285 StartZ=0 EndX=42.5 EndY=285 EndZ=0
    g3: LineSegment StartX=0 StartY=377 StartZ=0 EndX=27.5 EndY=377 EndZ=0
    g4: LineSegment StartX=0 StartY=285 StartZ=0 EndX=0 EndY=377 EndZ=0
  constraints (13):
    c: Coincident(g2,g0)
    c: Vertical(g0)
    c: Coincident(g2,g-3)
    c: Tangent(g0,g1) = -1.5708
    c: PointOnObject(g2,g-2)
    c: PointOnObject(g2,g-3)
    c: PointOnObject(g3,g-2)
    c: Horizontal(g3)
    c: Tangent(g3,g1) = 1.5708
    c: Coincident(g4,g2)
    c: Coincident(g4,g3)
    c: DistanceY(g4,g4) = 92
    c: Radius(g1) = 15
FEATURE [PartDesign::SubShapeBinder] Binder120
  BindCopyOnChange = 0
  BindMode = 0
  ClaimChildren = false
  Context = -> Body107 [Binder120.]
  Fuse = false
  MakeFace = true
  OffsetFill = false
  OffsetIntersection = false
  OffsetJoinType = 0
  OffsetOpenResult = false
  PartialLoad = false
  Relative = true
  Support = -> [Body007[Binder063.]]
  _Version = 2
FEATURE [PartDesign::Pocket] Pocket110
  BaseFeature = -> Mirrored011
  Direction = (0,0,-1)
  Length = 5
  Length2 = 5
  Profile = -> Binder120
  Suppressed = false
  Type = 1
FEATURE [PartDesign::SubShapeBinder] Binder121
  BindCopyOnChange = 0
  BindMode = 0
  ClaimChildren = false
  Context = -> Body107 [Binder121.]
  Fuse = false
  MakeFace = true
  OffsetFill = false
  OffsetIntersection = false
  OffsetJoinType = 0
  OffsetOpenResult = false
  PartialLoad = false
  Relative = true
  Support = -> [Body007[Pocket057.Sketch110.,Pocket058.Sketch111.]]
  _Version = 2
FEATURE [PartDesign::Pocket] Pocket111
  BaseFeature = -> Pocket110
  Direction = (0,0,-1)
  Length = 5
  Length2 = 5
  Midplane = true
  Profile = -> Binder121
  Suppressed = false
  Type = 1
FEATURE [PartDesign::Mirrored] Mirrored012
  BaseFeature = -> Pocket111
  MirrorPlane = -> YZ_Plane080
  Originals = -> [Pocket110]
  Suppressed = false
FEATURE [PartDesign::FeatureAdditivePython] PDW_Add  # link proxy (typed FeaturePython)
  BaseFeature = -> Mirrored012
  Body = Body107
  ClaimChildren = false
  EditPlacementAdjustments = false
  Enabled = 1
  LinkedObject = -> Mirrored011
  MeshTolerance = 0.1
  PatternBase = -> Mirrored012
  PatternBaseOffset = 0
  PatternBaseScale = 1
  PatternBaseScaleXYZ = (1,1,1)
  PatternOffsetCut = false
  PatternOffsetIntersection = false
  PatternOffsetJoin = 0
  PatternOffsetMode = 0
  PatternOffsetSelfIntersection = false
  PatternOperation = 0
  PatternOperationDefault = None
  PatternScaleCut = false
  PatternShapeOffset = 0
  PatternShapeScale = 1
  PatternShapeScaleXYZ = (1,1,1)
  PatternTool = -> Mirrored011
  PatternToolOffset = 0
  PatternToolScale = 1
  PatternToolScaleXYZ = (1,1,1)
  RefineMesh = true
  ShapeManagement = 0
  ShowMeshProps = false
  ShowOffsetProps = false
  ShowScaleProps = false
  ShowWarnings = true
  Suppressed = false
  TipBase = -> Mirrored012
  TipBaseOffset = 0
  TipBaseScale = 1
  TipBaseScaleXYZ = (1,1,1)
  TipOffsetCut = false
  TipOffsetIntersection = false
  TipOffsetJoin = 0
  TipOffsetMode = 0
  TipOffsetSelfIntersection = false
  TipOperation = 0
  TipOperationDefault = Fuse
  TipScaleCut = false
  TipShapeOffset = 0
  TipShapeScale = 1
  TipShapeScaleXYZ = (1,1,1)
  TipTool = -> Mirrored011
  TipToolOffset = 0
  TipToolScale = 1
  TipToolScaleXYZ = (1,1,1)
  Type = Additive
  UsePatternBaseAddSubShape = false
  UsePatternToolAddSubShape = true
  UseTipBaseAddSubShape = false
  UseTipToolAddSubShape = true
  Version = 0.2023.08.13
FEATURE [PartDesign::FeatureAdditivePython] PDW_Common_Add001  # link proxy (typed FeaturePython)
  BaseFeature = -> PDW_Add
  Body = Body107
  ClaimChildren = false
  EditPlacementAdjustments = false
  Enabled = 1
  LinkedObject = -> Mirrored012
  MeshTolerance = 0.1
  PatternBase = -> PDW_Add
  PatternBaseOffset = 0
  PatternBaseScale = 1
  PatternBaseScaleXYZ = (1,1,1)
  PatternOffsetCut = false
  PatternOffsetIntersection = false
  PatternOffsetJoin = 0
  PatternOffsetMode = 0
  PatternOffsetSelfIntersection = false
  PatternOperation = 3
  PatternOperationDefault = Common
  PatternScaleCut = false
  PatternShapeOffset = 0
  PatternShapeScale = 1
  PatternShapeScaleXYZ = (1,1,1)
  PatternTool = -> Mirrored012
  PatternToolOffset = 0
  PatternToolScale = 1
  PatternToolScaleXYZ = (1,1,1)
  RefineMesh = true
  ShapeManagement = 0
  ShowMeshProps = false
  ShowOffsetProps = false
  ShowScaleProps = false
  ShowWarnings = true
  Suppressed = false
  TipBase = -> PDW_Add
  TipBaseOffset = 0
  TipBaseScale = 1
  TipBaseScaleXYZ = (1,1,1)
  TipOffsetCut = false
  TipOffsetIntersection = false
  TipOffsetJoin = 0
  TipOffsetMode = 0
  TipOffsetSelfIntersection = false
  TipOperation = 2
  TipOperationDefault = Common
  TipScaleCut = false
  TipShapeOffset = 0
  TipShapeScale = 1
  TipShapeScaleXYZ = (1,1,1)
  TipTool = -> Mirrored012
  TipToolOffset = 0
  TipToolScale = 1
  TipToolScaleXYZ = (1,1,1)
  Type = Additive
  UsePatternBaseAddSubShape = false
  UsePatternToolAddSubShape = true
  UseTipBaseAddSubShape = false
  UseTipToolAddSubShape = true
  Version = 0.2023.08.13
FEATURE [PartDesign::PolarPattern] PolarPattern007
  Angle = 360
  Axis = -> Z_Axis080
  BaseFeature = -> PDW_Common_Add001
  Mode = 0
  Occurrences = 3
  Offset = 120
  Originals = -> [PDW_Common_Add001]
  Refine = true
  Suppressed = false
FEATURE [PartDesign::Pocket] Pocket106
  BaseFeature = -> PolarPattern007
  Direction = (0,0,-1)
  Length = 5
  Length2 = 5
  Midplane = true
  Profile = -> Binder117
  Suppressed = false
  Type = 1
FEATURE [Sketcher::SketchObject] Sketch195
  AttachmentSupport = -> [XY_Plane080]
  ExternalGeometry = -> [Sketch174,Sketch171]
  FullyConstrained = true
  MapMode = 5
  sketch-geometry (9):
    g0: LineSegment StartX=6.08e-14 StartY=555.654 StartZ=0 EndX=42.5 EndY=285 EndZ=0
    g1: LineSegment StartX=42.5 StartY=285 StartZ=0 EndX=0 EndY=285 EndZ=0
    g2: LineSegment StartX=6.08e-14 StartY=555.654 StartZ=0 EndX=0 EndY=555.654 EndZ=0
    g3: LineSegment StartX=0 StartY=555.654 StartZ=0 EndX=0 EndY=285 EndZ=0
    g4: Circle CenterX=36 CenterY=265 CenterZ=0 NormalX=0 NormalY=0 NormalZ=1 AngleXU=0 Radius=2.5
    g5: Circle CenterX=68.9742 CenterY=55.7258 CenterZ=0 NormalX=0 NormalY=0 NormalZ=1 AngleXU=0 Radius=2.5
    g6: Circle CenterX=56.173 CenterY=140.207 CenterZ=0 NormalX=0 NormalY=0 NormalZ=1 AngleXU=0 Radius=2.5
    g7: LineSegment StartX=68.9742 StartY=55.7258 StartZ=0 EndX=56.173 EndY=140.207 EndZ=0
    g8: LineSegment StartX=56.173 StartY=140.207 StartZ=0 EndX=36 EndY=265 EndZ=0
  constraints (24):
    c: Coincident(g-3,g0)
    c: Coincident(g0,g-4)
    c: Coincident(g0,g1)
    c: Coincident(g0,g2)
    c: PointOnObject(g2,g-2)
    c: Horizontal(g2)
    c: Coincident(g2,g3)
    c: PointOnObject(g3,g-4)
    c: Vertical(g3)
    c: Coincident(g1,g3)
    c: Diameter(g4) = 5
    c: DistanceX(g-1,g4) = 36
    c: DistanceY(g-1,g4) = 265
    c: Equal(g5,g6)
    c: Equal(g6,g4)
    c: Block(g5)
    c: Block(g6)
    c: Coincident(g7,g5)
    c: Coincident(g7,g6)
    c: Coincident(g8,g6)
    c: Coincident(g8,g4)
    c: DistanceX(g5) = 68.9742
    c: DistanceY(g5) = 55.7258
    c: Distance(g6,g-3) = 419.132
FEATURE [PartDesign::Boolean] Boolean027
  BaseFeature = -> Pocket106
  Group = -> [Populate041,Cylinder012]
  Suppressed = false
  Type = 1
  UsePlacement = false
FEATURE [PartDesign::CoordinateSystem] Local_CS014  label="basement_bottom_amplifier_bottom_LCS"
  AttacherType = Attacher::AttachEngine3D
  AttachmentSupport = -> [XY_Plane080]
  MapMode = 5
FEATURE [PartDesign::CoordinateSystem] Local_CS015  label="basement_bottom_amplifier_top_LCS"
  AttacherType = Attacher::AttachEngine3D
  AttachmentOffset = pos=(0,0,2) rot=(0,0,1;0rad)
  AttachmentSupport = -> [XY_Plane080]
  MapMode = 5
  Placement = pos=(0,0,2) rot=(0,0,1;0rad)
FEATURE [PartDesign::CoordinateSystem] Local_CS048
  AttacherType = Attacher::AttachEngine3D
  AttachmentOffset = pos=(0,0,0) rot=(0,1,0;1.5708rad)
  AttachmentSupport = -> [Sketch171]
  MapMode = 7
  Placement = pos=(42.5,285,0) rot=(0.517473,0.605071,0.605071;2.18654rad)
FEATURE [Sketcher::SketchObject] Sketch272
  AttachmentSupport = -> [Local_CS048]
  FullyConstrained = true
  MapMode = 5
  Placement = pos=(42.5,285,0) rot=(0.517473,0.605071,0.605071;2.18654rad)
FEATURE [PartDesign::Body] Body107  label="basement_bottom_amplifier_material_0.50ansi"
  Group = -> [Sketch171,BaseBend044,Bend026,Sketch174,Binder117,Pocket105,Sketch176,Binder120,Local_CS048,Sketch272,Mirrored011,Pocket110,Binder121,Pocket111,Sketch195,Mirrored012,PDW_Add,PDW_Common_Add001,PolarPattern007,Pocket106,Boolean027,Local_CS014,Local_CS015]
  Origin = -> Origin080
  Tip = -> Boolean027
COMPONENT P61 — recipe-attached ("basement2_plywood001", modeled in this document).
Construction recipe (the document's own serialized feature program — sketch geometry with constraints, then the solid features built on it; lengths are millimeters unless a unit is written):

FEATURE [PartDesign::SubShapeBinder] Binder003
  BindCopyOnChange = 0
  BindMode = 0
  ClaimChildren = true
  Context = -> Body007 [Binder003.]
  Fuse = false
  MakeFace = true
  OffsetFill = false
  OffsetIntersection = false
  OffsetJoinType = 0
  OffsetOpenResult = false
  PartialLoad = false
  Relative = false
  Support = -> [Array002]
  _Version = 2
FEATURE [PartDesign::Pad] Pad002
  Direction = (0,0,1)
  Length = 18
  Length2 = 10
  Profile = -> Binder003
  Suppressed = false
  Type = 0
FEATURE [Sketcher::SketchObject] Sketch110
  AttachmentOffset = pos=(0,333,0) rot=(0,0,1;0rad)
  AttachmentSupport = -> [XY_Plane011]
  FullyConstrained = true
  MapMode = 5
  Placement = pos=(0,333,0) rot=(0,0,1;0rad)
  sketch-geometry (2):
    g0: Circle CenterX=0 CenterY=26.3 CenterZ=0 NormalX=0 NormalY=0 NormalZ=1 AngleXU=0 Radius=2.75
    g1: Circle CenterX=0 CenterY=-26.3 CenterZ=0 NormalX=0 NormalY=0 NormalZ=1 AngleXU=0 Radius=2.75
  constraints (5):
    c: PointOnObject(g0,g-2)
    c: Equal(g1,g0)
    c: Diameter(g1) = 5.5
    c: Symmetric(g1,g0,g-1)
    c: DistanceY(g1,g0) = 52.6
FEATURE [PartDesign::PolarPattern] PolarPattern002
  Angle = 360
  Axis = -> Z_Axis011
  BaseFeature = -> Pad002
  Mode = 0
  Occurrences = 3
  Offset = 120
  Suppressed = false
FEATURE [Sketcher::SketchObject] Sketch178
  AttachmentSupport = -> [XY_Plane011]
  FullyConstrained = true
  MapMode = 5
  sketch-geometry (4):
    g0: Circle CenterX=29 CenterY=-145.633 CenterZ=0 NormalX=0 NormalY=0 NormalZ=1 AngleXU=0 Radius=4.25
    g1: LineSegment StartX=0 StartY=0 StartZ=0 EndX=84.8108 EndY=-48.9655 EndZ=0
    g2: Circle CenterX=140.622 CenterY=47.7016 CenterZ=0 NormalX=0 NormalY=0 NormalZ=1 AngleXU=0 Radius=4.25
    g3: LineSegment StartX=140.622 StartY=47.7016 StartZ=0 EndX=29 EndY=-145.633 EndZ=0
  constraints (10):
    c: Diameter(g0) = 8.5
    c: DistanceX(g0) = 29
    c: DistanceY(g0) = -145.633
    c: Coincident(g1,g-1)
    c: Angle(g1) = -0.523599
    c: Symmetric(g2,g0,g1)
    c: Equal(g2,g0)
    c: Coincident(g3,g2)
    c: Coincident(g3,g0)
    c: PointOnObject(g1,g3)
FEATURE [Sketcher::SketchObject] Sketch218
  AttachmentOffset = pos=(0,0,18) rot=(0,0,1;0rad)
  AttachmentSupport = -> [XY_Plane011]
  FullyConstrained = false
  MapMode = 5
  Placement = pos=(0,0,18) rot=(0,0,1;0rad)
  sketch-geometry (4):
    g0: LineSegment StartX=93.4507 StartY=-44.023 StartZ=0 EndX=107.489 EndY=-44.023 EndZ=0
    g1: LineSegment StartX=107.489 StartY=-44.023 StartZ=0 EndX=107.489 EndY=-29.1068 EndZ=0
    g2: LineSegment StartX=107.489 StartY=-29.1068 StartZ=0 EndX=93.4507 EndY=-29.1068 EndZ=0
    g3: LineSegment StartX=93.4507 StartY=-29.1068 StartZ=0 EndX=93.4507 EndY=-44.023 EndZ=0
  constraints (8):
    c: Coincident(g0,g1)
    c: Coincident(g1,g2)
    c: Coincident(g2,g3)
    c: Coincident(g3,g0)
    c: Horizontal(g0)
    c: Horizontal(g2)
    c: Vertical(g1)
    c: Vertical(g3)
FEATURE [PartDesign::Boolean] Boolean026
  BaseFeature = -> Pad002
  Group = -> [Compound069]
  Suppressed = false
  Type = 1
  UsePlacement = false
FEATURE [PartDesign::CoordinateSystem] Local_CS010  label="basement_bottom_plywood_bottom"
  AttacherType = Attacher::AttachEngine3D
  AttachmentSupport = -> [XY_Plane011]
  MapMode = 5
FEATURE [PartDesign::CoordinateSystem] Local_CS011  label="basement_bottom_plywood_top"
  AttacherType = Attacher::AttachEngine3D
  AttachmentOffset = pos=(0,0,18) rot=(0,0,1;0rad)
  AttachmentSupport = -> [XY_Plane011]
  MapMode = 5
  Placement = pos=(0,0,18) rot=(0,0,1;0rad)
FEATURE [PartDesign::Body] Body007  label="basement_bottom_plywood"
  Group = -> [Binder003,Pad002,Sketch110,PolarPattern002,Sketch178,Boolean026,Sketch218,Local_CS010,Local_CS011]
  Origin = -> Origin011
  Tip = -> Boolean026
COMPONENT P62 — recipe-attached ("basement2_proxy001", modeled in this document).
Construction recipe (the document's own serialized feature program — sketch geometry with constraints, then the solid features built on it; lengths are millimeters unless a unit is written):

FEATURE [PartDesign::SubShapeBinder] Binder004
  BindCopyOnChange = 0
  BindMode = 0
  ClaimChildren = true
  Context = -> Body009 [Binder004.]
  Fuse = false
  MakeFace = true
  Offset = 2
  OffsetFill = false
  OffsetIntersection = false
  OffsetJoinType = 0
  OffsetOpenResult = false
  PartialLoad = false
  Relative = false
  Support = -> [Array002]
  _Version = 2
FEATURE [PartDesign::Pad] Pad004
  Direction = (0,0,1)
  Length = 3
  Length2 = 10
  Profile = -> Binder004
  Suppressed = false
  Type = 0
FEATURE [PartDesign::SubShapeBinder] Binder134
  BindCopyOnChange = 0
  BindMode = 0
  ClaimChildren = false
  Context = -> Body009 [Binder134.]
  Fuse = false
  MakeFace = true
  OffsetFill = false
  OffsetIntersection = false
  OffsetJoinType = 0
  OffsetOpenResult = false
  PartialLoad = false
  Relative = true
  Support = -> [Body007[Pocket112.Sketch178.]]
  _Version = 2
FEATURE [PartDesign::Boolean] Boolean029
  BaseFeature = -> Pad004
  Group = -> [Compound071]
  Suppressed = false
  Type = 1
  UsePlacement = false
FEATURE [PartDesign::CoordinateSystem] Local_CS012  label="basement_bottom_proxy_bottom"
  AttacherType = Attacher::AttachEngine3D
  AttachmentSupport = -> [XY_Plane013]
  MapMode = 5
FEATURE [PartDesign::CoordinateSystem] Local_CS013  label="basement_bottom_proxy_top"
  AttacherType = Attacher::AttachEngine3D
  AttachmentOffset = pos=(0,0,3) rot=(0,0,1;0rad)
  AttachmentSupport = -> [XY_Plane013]
  MapMode = 5
  Placement = pos=(0,0,3) rot=(0,0,1;0rad)
FEATURE [PartDesign::CoordinateSystem] Local_CS016  label="basement_bottom_proxy_pillar_back_LCS"
  AttacherType = Attacher::AttachEngine3D
  AttachmentOffset = pos=(0,384,3) rot=(0,0,-1;3.14159rad)
  AttachmentSupport = -> [XY_Plane013]
  MapMode = 5
  Placement = pos=(0,384,3) rot=(0,0,-1;3.14159rad)
  expr: .AttachmentOffset.Base.y = <<pillar_placement>>.Placement.Base.y
FEATURE [PartDesign::CoordinateSystem] Local_CS023  label="basement_bottom_proxy_pillar_left_LCS"
  AttacherType = Attacher::AttachEngine3D
  AttachmentOffset = pos=(-332.554,-192,3) rot=(0,0,-1;1.0472rad)
  AttachmentSupport = -> [XY_Plane013]
  MapMode = 5
  Placement = pos=(-332.554,-192,3) rot=(0,0,-1;1.0472rad)
  expr: .AttachmentOffset.Base.x = <<pillar_placement>>.Placement.Base.y * cos(210)
  expr: .AttachmentOffset.Base.y = <<pillar_placement>>.Placement.Base.y * sin(210)
FEATURE [PartDesign::CoordinateSystem] Local_CS024  label="basement_bottom_proxy_pillar_right_LCS"
  AttacherType = Attacher::AttachEngine3D
  AttachmentOffset = pos=(332.554,-192,3) rot=(0,0,1;1.0472rad)
  AttachmentSupport = -> [XY_Plane013]
  MapMode = 5
  Placement = pos=(332.554,-192,3) rot=(0,0,1;1.0472rad)
  expr: .AttachmentOffset.Base.x = <<pillar_placement>>.Placement.Base.y * cos(330)
  expr: .AttachmentOffset.Base.y = <<pillar_placement>>.Placement.Base.y * sin(330)
FEATURE [PartDesign::Body] Body009  label="basement_bottom_proxy"
  Group = -> [Binder004,Pad004,Binder134,Boolean029,Local_CS012,Local_CS013,Local_CS016,Local_CS023,Local_CS024]
  Origin = -> Origin013
  Tip = -> Boolean029
